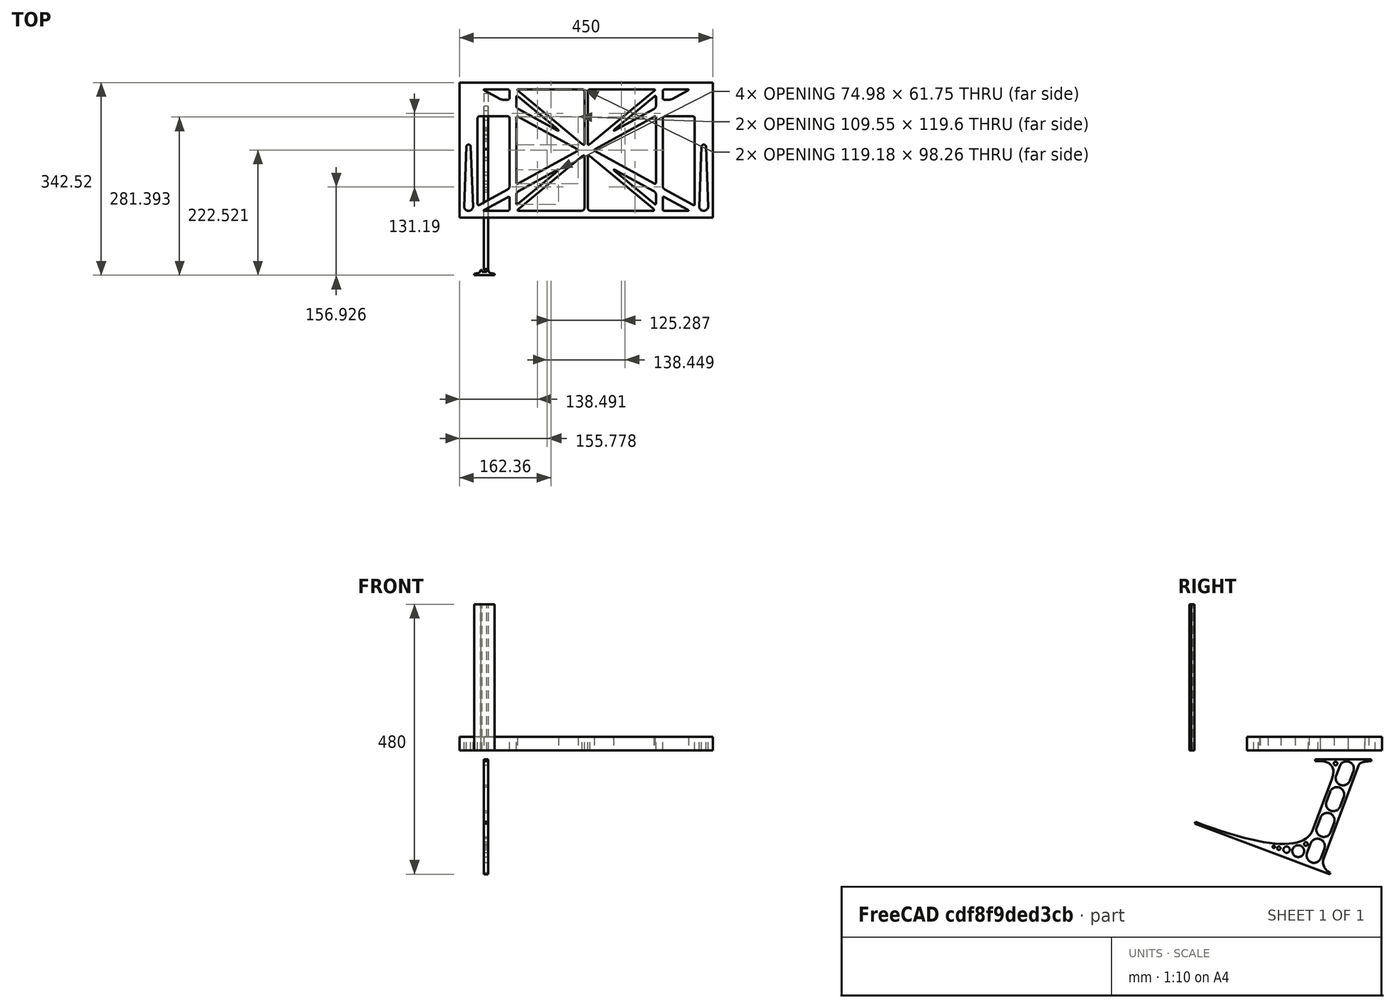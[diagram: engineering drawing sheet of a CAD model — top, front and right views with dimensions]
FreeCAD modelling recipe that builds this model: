
FCSTD DOCUMENT  (FreeCAD 0.19R0.19.2)
Label: laptopStand159FCStd
License: All rights reserved
LicenseURL: http://en.wikipedia.org/wiki/All_rights_reserved
objects: Sketcher::SketchObject×4, Part::Extrusion×3
note: 7 computed .brp shape members not serialized (recipe doc carries the construction recipe); baked Part::Feature solids carry a one-line shape summary decoded from their .brp

FEATURE [Sketcher::SketchObject] Sketch
  FullyConstrained = false
  sketch-geometry (349):
    g0: LineSegment StartX=-10.9272 StartY=-82.7794 StartZ=0 EndX=46.0728 EndY=-51.4823 EndZ=0
    g1: LineSegment StartX=-10.9272 StartY=76.4095 StartZ=0 EndX=-10.9272 EndY=-82.7794 EndZ=0
    g2: LineSegment StartX=46.0728 StartY=76.4095 StartZ=0 EndX=46.0728 EndY=-51.4823 EndZ=0
    g3: LineSegment StartX=-42.9272 StartY=136.221 StartZ=0 EndX=-42.9272 EndY=-103.779 EndZ=0
    g4: LineSegment StartX=407.073 StartY=136.221 StartZ=0 EndX=407.073 EndY=-103.779 EndZ=0
    g5: ArcOfCircle CenterX=-26.9272 CenterY=-83.7794 CenterZ=0 NormalX=0 NormalY=0 NormalZ=1 AngleXU=0 Radius=8 StartAngle=3.14159 EndAngle=6.28319
    g6: ArcOfCircle CenterX=391.073 CenterY=22.1087 CenterZ=0 NormalX=0 NormalY=0 NormalZ=1 AngleXU=0 Radius=8 StartAngle=-4.4e-15 EndAngle=3.14159
    g7: LineSegment StartX=399.073 StartY=22.1087 StartZ=0 EndX=399.073 EndY=-83.7794 EndZ=0
    g8: LineSegment StartX=383.073 StartY=22.1087 StartZ=0 EndX=383.073 EndY=-83.7794 EndZ=0
    g9: ArcOfCircle CenterX=391.073 CenterY=-83.7794 CenterZ=0 NormalX=0 NormalY=0 NormalZ=1 AngleXU=0 Radius=8 StartAngle=3.14159 EndAngle=6.28319
    g10: Circle CenterX=175.022 CenterY=27.0628 CenterZ=0 NormalX=0 NormalY=0 NormalZ=1 AngleXU=0 Radius=1
    g11: Circle CenterX=179.022 CenterY=24.8665 CenterZ=0 NormalX=0 NormalY=0 NormalZ=1 AngleXU=0 Radius=1
    g12: Circle CenterX=179.022 CenterY=27.0628 CenterZ=0 NormalX=0 NormalY=0 NormalZ=1 AngleXU=0 Radius=1
    g13: BSplineCurve PolesCount=3 KnotsCount=2 Degree=2 IsPeriodic=0
    g14: GeomPoint X=175.022 Y=27.0628 Z=0
    g15: GeomPoint X=179.022 Y=27.0628 Z=0
    g16: Circle CenterX=189.124 CenterY=27.0628 CenterZ=0 NormalX=0 NormalY=0 NormalZ=1 AngleXU=0 Radius=1
    g17: Circle CenterX=185.124 CenterY=24.8665 CenterZ=0 NormalX=0 NormalY=0 NormalZ=1 AngleXU=0 Radius=1
    g18: Circle CenterX=185.124 CenterY=27.0628 CenterZ=0 NormalX=0 NormalY=0 NormalZ=1 AngleXU=0 Radius=1
    g19: BSplineCurve PolesCount=3 KnotsCount=2 Degree=2 IsPeriodic=0
    g20: GeomPoint X=189.124 Y=27.0628 Z=0
    g21: GeomPoint X=185.124 Y=27.0628 Z=0
    g22: Circle CenterX=175.022 CenterY=5.37834 CenterZ=0 NormalX=0 NormalY=0 NormalZ=1 AngleXU=0 Radius=1
    g23: Circle CenterX=179.022 CenterY=7.57463 CenterZ=0 NormalX=0 NormalY=0 NormalZ=1 AngleXU=0 Radius=1
    g24: Circle CenterX=179.022 CenterY=5.34704 CenterZ=0 NormalX=0 NormalY=0 NormalZ=1 AngleXU=0 Radius=1
    g25: BSplineCurve PolesCount=3 KnotsCount=2 Degree=2 IsPeriodic=0
    g26: GeomPoint X=175.022 Y=5.37834 Z=0
    g27: GeomPoint X=179.022 Y=5.34704 Z=0
    g28: Circle CenterX=189.124 CenterY=5.37834 CenterZ=0 NormalX=0 NormalY=0 NormalZ=1 AngleXU=0 Radius=1
    g29: Circle CenterX=185.124 CenterY=7.57463 CenterZ=0 NormalX=0 NormalY=0 NormalZ=1 AngleXU=0 Radius=1
    g30: Circle CenterX=185.124 CenterY=5.34704 CenterZ=0 NormalX=0 NormalY=0 NormalZ=1 AngleXU=0 Radius=1
    g31: BSplineCurve PolesCount=3 KnotsCount=2 Degree=2 IsPeriodic=0
    g32: GeomPoint X=189.124 Y=5.37834 Z=0
    g33: GeomPoint X=185.124 Y=5.34704 Z=0
    g34: Circle CenterX=165.871 CenterY=18.1458 CenterZ=0 NormalX=0 NormalY=0 NormalZ=1 AngleXU=0 Radius=1
    g35: Circle CenterX=169.377 CenterY=16.2206 CenterZ=0 NormalX=0 NormalY=0 NormalZ=1 AngleXU=0 Radius=1
    g36: Circle CenterX=165.871 CenterY=14.2954 CenterZ=0 NormalX=0 NormalY=0 NormalZ=1 AngleXU=0 Radius=1
    g37: BSplineCurve PolesCount=3 KnotsCount=2 Degree=2 IsPeriodic=0
    g38: GeomPoint X=165.871 Y=18.1458 Z=0
    g39: GeomPoint X=165.871 Y=14.2954 Z=0
    g40: Circle CenterX=198.275 CenterY=18.1458 CenterZ=0 NormalX=0 NormalY=0 NormalZ=1 AngleXU=0 Radius=1
    g41: Circle CenterX=194.768 CenterY=16.2206 CenterZ=0 NormalX=0 NormalY=0 NormalZ=1 AngleXU=0 Radius=1
    g42: Circle CenterX=198.275 CenterY=14.2954 CenterZ=0 NormalX=0 NormalY=0 NormalZ=1 AngleXU=0 Radius=1
    g43: BSplineCurve PolesCount=3 KnotsCount=2 Degree=2 IsPeriodic=0
    g44: GeomPoint X=198.275 Y=18.1458 Z=0
    g45: GeomPoint X=198.275 Y=14.2954 Z=0
    g46: LineSegment StartX=407.073 StartY=-103.779 StartZ=0 EndX=-42.9272 EndY=-103.779 EndZ=0
    g47: LineSegment StartX=407.073 StartY=136.221 StartZ=0 EndX=-42.9272 EndY=136.221 EndZ=0
    g48: LineSegment StartX=46.0728 StartY=76.4095 StartZ=0 EndX=-10.9272 EndY=76.4095 EndZ=0
    g49: Circle CenterX=125.607 CenterY=54.1951 CenterZ=0 NormalX=0 NormalY=0 NormalZ=1 AngleXU=0 Radius=1
    g50: Circle CenterX=139.632 CenterY=46.4944 CenterZ=0 NormalX=0 NormalY=0 NormalZ=1 AngleXU=0 Radius=1
    g51: Circle CenterX=127.326 CenterY=56.7187 CenterZ=0 NormalX=0 NormalY=0 NormalZ=1 AngleXU=0 Radius=1
    g52: BSplineCurve PolesCount=3 KnotsCount=2 Degree=2 IsPeriodic=0
    g53: GeomPoint X=125.607 Y=54.1951 Z=0
    g54: GeomPoint X=127.326 Y=56.7187 Z=0
    g55: Circle CenterX=236.821 CenterY=56.7187 CenterZ=0 NormalX=0 NormalY=0 NormalZ=1 AngleXU=0 Radius=1
    g56: Circle CenterX=224.513 CenterY=46.4944 CenterZ=0 NormalX=0 NormalY=0 NormalZ=1 AngleXU=0 Radius=1
    g57: Circle CenterX=238.538 CenterY=54.1951 CenterZ=0 NormalX=0 NormalY=0 NormalZ=1 AngleXU=0 Radius=1
    g58: BSplineCurve PolesCount=3 KnotsCount=2 Degree=2 IsPeriodic=0
    g59: GeomPoint X=236.821 Y=56.7187 Z=0
    g60: GeomPoint X=238.538 Y=54.1951 Z=0
    g61: Circle CenterX=238.538 CenterY=-21.7539 CenterZ=0 NormalX=0 NormalY=0 NormalZ=1 AngleXU=0 Radius=1
    g62: Circle CenterX=224.513 CenterY=-14.0532 CenterZ=0 NormalX=0 NormalY=0 NormalZ=1 AngleXU=0 Radius=1
    g63: Circle CenterX=236.821 CenterY=-24.2775 CenterZ=0 NormalX=0 NormalY=0 NormalZ=1 AngleXU=0 Radius=1
    g64: BSplineCurve PolesCount=3 KnotsCount=2 Degree=2 IsPeriodic=0
    g65: GeomPoint X=238.538 Y=-21.7539 Z=0
    g66: GeomPoint X=236.821 Y=-24.2775 Z=0
    g67: Circle CenterX=125.607 CenterY=-21.7539 CenterZ=0 NormalX=0 NormalY=0 NormalZ=1 AngleXU=0 Radius=1
    g68: Circle CenterX=139.632 CenterY=-14.0532 CenterZ=0 NormalX=0 NormalY=0 NormalZ=1 AngleXU=0 Radius=1
    g69: Circle CenterX=127.325 CenterY=-24.2775 CenterZ=0 NormalX=0 NormalY=0 NormalZ=1 AngleXU=0 Radius=1
    g70: BSplineCurve PolesCount=3 KnotsCount=2 Degree=2 IsPeriodic=0
    g71: GeomPoint X=125.607 Y=-21.7539 Z=0
    g72: GeomPoint X=127.325 Y=-24.2775 Z=0
    g73: Circle CenterX=302.996 CenterY=111.695 CenterZ=0 NormalX=0 NormalY=0 NormalZ=1 AngleXU=0 Radius=1
    g74: Circle CenterX=306.073 CenterY=114.251 CenterZ=0 NormalX=0 NormalY=0 NormalZ=1 AngleXU=0 Radius=1
    g75: Circle CenterX=306.073 CenterY=110.251 CenterZ=0 NormalX=0 NormalY=0 NormalZ=1 AngleXU=0 Radius=1
    g76: BSplineCurve PolesCount=3 KnotsCount=2 Degree=2 IsPeriodic=0
    g77: GeomPoint X=302.996 Y=111.695 Z=0
    g78: GeomPoint X=306.073 Y=110.251 Z=0
    g79: Circle CenterX=306.073 CenterY=95.2763 CenterZ=0 NormalX=0 NormalY=0 NormalZ=1 AngleXU=0 Radius=1
    g80: Circle CenterX=306.073 CenterY=91.2763 CenterZ=0 NormalX=0 NormalY=0 NormalZ=1 AngleXU=0 Radius=1
    g81: Circle CenterX=302.567 CenterY=89.3511 CenterZ=0 NormalX=0 NormalY=0 NormalZ=1 AngleXU=0 Radius=1
    g82: BSplineCurve PolesCount=3 KnotsCount=2 Degree=2 IsPeriodic=0
    g83: GeomPoint X=306.073 Y=95.2763 Z=0
    g84: GeomPoint X=302.567 Y=89.3511 Z=0
    g85: LineSegment StartX=306.073 StartY=110.251 StartZ=0 EndX=306.073 EndY=95.2763 EndZ=0
    g86: LineSegment StartX=302.996 StartY=111.695 StartZ=0 EndX=236.821 EndY=56.7187 EndZ=0
    g87: LineSegment StartX=238.538 StartY=54.1951 StartZ=0 EndX=302.567 EndY=89.3511 EndZ=0
    g88: Circle CenterX=61.1496 CenterY=111.695 CenterZ=0 NormalX=0 NormalY=0 NormalZ=1 AngleXU=0 Radius=1
    g89: Circle CenterX=58.0728 CenterY=114.251 CenterZ=0 NormalX=0 NormalY=0 NormalZ=1 AngleXU=0 Radius=1
    g90: Circle CenterX=58.0728 CenterY=110.251 CenterZ=0 NormalX=0 NormalY=0 NormalZ=1 AngleXU=0 Radius=1
    g91: BSplineCurve PolesCount=3 KnotsCount=2 Degree=2 IsPeriodic=0
    g92: GeomPoint X=61.1496 Y=111.695 Z=0
    g93: GeomPoint X=58.0728 Y=110.251 Z=0
    g94: Circle CenterX=61.5791 CenterY=89.3511 CenterZ=0 NormalX=0 NormalY=0 NormalZ=1 AngleXU=0 Radius=1
    g95: Circle CenterX=58.0728 CenterY=91.2763 CenterZ=0 NormalX=0 NormalY=0 NormalZ=1 AngleXU=0 Radius=1
    g96: Circle CenterX=58.0728 CenterY=95.2763 CenterZ=0 NormalX=0 NormalY=0 NormalZ=1 AngleXU=0 Radius=1
    g97: BSplineCurve PolesCount=3 KnotsCount=2 Degree=2 IsPeriodic=0
    g98: GeomPoint X=61.5791 Y=89.3511 Z=0
    g99: GeomPoint X=58.0728 Y=95.2763 Z=0
    g100: LineSegment StartX=58.0728 StartY=110.251 StartZ=0 EndX=58.0728 EndY=95.2763 EndZ=0
    g101: LineSegment StartX=61.1496 StartY=111.695 StartZ=0 EndX=127.326 EndY=56.7187 EndZ=0
    g102: LineSegment StartX=125.607 StartY=54.1951 StartZ=0 EndX=61.5791 EndY=89.3511 EndZ=0
    g103: Circle CenterX=61.5791 CenterY=-56.9099 CenterZ=0 NormalX=0 NormalY=0 NormalZ=1 AngleXU=0 Radius=1
    g104: Circle CenterX=58.0728 CenterY=-58.8351 CenterZ=0 NormalX=0 NormalY=0 NormalZ=1 AngleXU=0 Radius=1
    g105: Circle CenterX=58.0728 CenterY=-62.8351 CenterZ=0 NormalX=0 NormalY=0 NormalZ=1 AngleXU=0 Radius=1
    g106: BSplineCurve PolesCount=3 KnotsCount=2 Degree=2 IsPeriodic=0
    g107: GeomPoint X=61.5791 Y=-56.9099 Z=0
    g108: GeomPoint X=58.0728 Y=-62.8351 Z=0
    g109: Circle CenterX=58.0728 CenterY=-77.8102 CenterZ=0 NormalX=0 NormalY=0 NormalZ=1 AngleXU=0 Radius=1
    g110: Circle CenterX=58.0728 CenterY=-81.8102 CenterZ=0 NormalX=0 NormalY=0 NormalZ=1 AngleXU=0 Radius=1
    g111: Circle CenterX=61.1496 CenterY=-79.2541 CenterZ=0 NormalX=0 NormalY=0 NormalZ=1 AngleXU=0 Radius=1
    g112: BSplineCurve PolesCount=3 KnotsCount=2 Degree=2 IsPeriodic=0
    g113: GeomPoint X=58.0728 Y=-77.8102 Z=0
    g114: GeomPoint X=61.1496 Y=-79.2541 Z=0
    g115: LineSegment StartX=58.0728 StartY=-62.8351 StartZ=0 EndX=58.0728 EndY=-77.8102 EndZ=0
    g116: LineSegment StartX=61.1496 StartY=-79.2541 StartZ=0 EndX=127.325 EndY=-24.2775 EndZ=0
    g117: LineSegment StartX=125.607 StartY=-21.7539 StartZ=0 EndX=61.5791 EndY=-56.9099 EndZ=0
    g118: Circle CenterX=302.567 CenterY=-56.9099 CenterZ=0 NormalX=0 NormalY=0 NormalZ=1 AngleXU=0 Radius=1
    g119: Circle CenterX=306.073 CenterY=-58.8351 CenterZ=0 NormalX=0 NormalY=0 NormalZ=1 AngleXU=0 Radius=1
    g120: Circle CenterX=306.073 CenterY=-62.8351 CenterZ=0 NormalX=0 NormalY=0 NormalZ=1 AngleXU=0 Radius=1
    g121: BSplineCurve PolesCount=3 KnotsCount=2 Degree=2 IsPeriodic=0
    g122: GeomPoint X=302.567 Y=-56.9099 Z=0
    g123: GeomPoint X=306.073 Y=-62.8351 Z=0
    g124: Circle CenterX=302.996 CenterY=-79.2541 CenterZ=0 NormalX=0 NormalY=0 NormalZ=1 AngleXU=0 Radius=1
    g125: Circle CenterX=306.073 CenterY=-81.8102 CenterZ=0 NormalX=0 NormalY=0 NormalZ=1 AngleXU=0 Radius=1
    g126: Circle CenterX=306.073 CenterY=-77.8102 CenterZ=0 NormalX=0 NormalY=0 NormalZ=1 AngleXU=0 Radius=1
    g127: BSplineCurve PolesCount=3 KnotsCount=2 Degree=2 IsPeriodic=0
    g128: GeomPoint X=302.996 Y=-79.2541 Z=0
    g129: GeomPoint X=306.073 Y=-77.8102 Z=0
    g130: LineSegment StartX=306.073 StartY=-62.8351 StartZ=0 EndX=306.073 EndY=-77.8102 EndZ=0
    g131: LineSegment StartX=302.996 StartY=-79.2541 StartZ=0 EndX=236.821 EndY=-24.2775 EndZ=0
    g132: LineSegment StartX=238.538 StartY=-21.7539 StartZ=0 EndX=302.567 EndY=-56.9099 EndZ=0
    g133: Circle CenterX=61.6457 CenterY=-88.8112 CenterZ=0 NormalX=0 NormalY=0 NormalZ=1 AngleXU=0 Radius=1
    g134: Circle CenterX=58.0728 CenterY=-91.7794 CenterZ=0 NormalX=0 NormalY=0 NormalZ=1 AngleXU=0 Radius=1
    g135: Circle CenterX=63.9135 CenterY=-91.7794 CenterZ=0 NormalX=0 NormalY=0 NormalZ=1 AngleXU=0 Radius=1
    g136: BSplineCurve PolesCount=3 KnotsCount=2 Degree=2 IsPeriodic=0
    g137: GeomPoint X=61.6457 Y=-88.8112 Z=0
    g138: GeomPoint X=63.9135 Y=-91.7794 Z=0
    g139: Circle CenterX=179.022 CenterY=-85.8163 CenterZ=0 NormalX=0 NormalY=0 NormalZ=1 AngleXU=0 Radius=1
    g140: Circle CenterX=179.022 CenterY=-91.7794 CenterZ=0 NormalX=0 NormalY=0 NormalZ=1 AngleXU=0 Radius=1
    g141: Circle CenterX=171.895 CenterY=-91.7794 CenterZ=0 NormalX=0 NormalY=0 NormalZ=1 AngleXU=0 Radius=1
    g142: BSplineCurve PolesCount=3 KnotsCount=2 Degree=2 IsPeriodic=0
    g143: GeomPoint X=179.022 Y=-85.8163 Z=0
    g144: GeomPoint X=171.895 Y=-91.7794 Z=0
    g145: Circle CenterX=185.124 CenterY=-86.2028 CenterZ=0 NormalX=0 NormalY=0 NormalZ=1 AngleXU=0 Radius=1
    g146: Circle CenterX=185.124 CenterY=-91.7794 CenterZ=0 NormalX=0 NormalY=0 NormalZ=1 AngleXU=0 Radius=1
    g147: Circle CenterX=191.747 CenterY=-91.7794 CenterZ=0 NormalX=0 NormalY=0 NormalZ=1 AngleXU=0 Radius=1
    g148: BSplineCurve PolesCount=3 KnotsCount=2 Degree=2 IsPeriodic=0
    g149: GeomPoint X=185.124 Y=-86.2028 Z=0
    g150: GeomPoint X=191.747 Y=-91.7794 Z=0
    g151: Circle CenterX=299.888 CenterY=-86.6413 CenterZ=0 NormalX=0 NormalY=0 NormalZ=1 AngleXU=0 Radius=1
    g152: Circle CenterX=306.073 CenterY=-91.7794 CenterZ=0 NormalX=0 NormalY=0 NormalZ=1 AngleXU=0 Radius=1
    g153: Circle CenterX=298.776 CenterY=-91.7794 CenterZ=0 NormalX=0 NormalY=0 NormalZ=1 AngleXU=0 Radius=1
    g154: BSplineCurve PolesCount=3 KnotsCount=2 Degree=2 IsPeriodic=0
    g155: GeomPoint X=299.888 Y=-86.6413 Z=0
    g156: GeomPoint X=298.776 Y=-91.7794 Z=0
    g157: LineSegment StartX=189.124 StartY=5.37834 StartZ=0 EndX=299.888 EndY=-86.6413 EndZ=0
    g158: LineSegment StartX=298.776 StartY=-91.7794 StartZ=0 EndX=191.747 EndY=-91.7794 EndZ=0
    g159: LineSegment StartX=185.124 StartY=-86.2028 StartZ=0 EndX=185.124 EndY=5.34704 EndZ=0
    g160: LineSegment StartX=179.022 StartY=5.34704 StartZ=0 EndX=179.022 EndY=-85.8163 EndZ=0
    g161: LineSegment StartX=171.895 StartY=-91.7794 StartZ=0 EndX=63.9135 EndY=-91.7794 EndZ=0
    g162: LineSegment StartX=61.6457 StartY=-88.8112 StartZ=0 EndX=175.022 EndY=5.37834 EndZ=0
    g163: Circle CenterX=302.073 CenterY=124.221 CenterZ=0 NormalX=0 NormalY=0 NormalZ=1 AngleXU=0 Radius=1
    g164: Circle CenterX=306.073 CenterY=124.221 CenterZ=0 NormalX=0 NormalY=0 NormalZ=1 AngleXU=0 Radius=1
    g165: Circle CenterX=302.996 CenterY=121.665 CenterZ=0 NormalX=0 NormalY=0 NormalZ=1 AngleXU=0 Radius=1
    g166: BSplineCurve PolesCount=3 KnotsCount=2 Degree=2 IsPeriodic=0
    g167: GeomPoint X=302.073 Y=124.221 Z=0
    g168: GeomPoint X=302.996 Y=121.665 Z=0
    g169: Circle CenterX=189.124 CenterY=124.221 CenterZ=0 NormalX=0 NormalY=0 NormalZ=1 AngleXU=0 Radius=1
    g170: Circle CenterX=185.124 CenterY=124.221 CenterZ=0 NormalX=0 NormalY=0 NormalZ=1 AngleXU=0 Radius=1
    g171: Circle CenterX=185.124 CenterY=120.221 CenterZ=0 NormalX=0 NormalY=0 NormalZ=1 AngleXU=0 Radius=1
    g172: BSplineCurve PolesCount=3 KnotsCount=2 Degree=2 IsPeriodic=0
    g173: GeomPoint X=189.124 Y=124.221 Z=0
    g174: GeomPoint X=185.124 Y=120.221 Z=0
    g175: Circle CenterX=175.022 CenterY=124.221 CenterZ=0 NormalX=0 NormalY=0 NormalZ=1 AngleXU=0 Radius=1
    g176: Circle CenterX=179.022 CenterY=124.221 CenterZ=0 NormalX=0 NormalY=0 NormalZ=1 AngleXU=0 Radius=1
    g177: Circle CenterX=179.022 CenterY=120.221 CenterZ=0 NormalX=0 NormalY=0 NormalZ=1 AngleXU=0 Radius=1
    g178: BSplineCurve PolesCount=3 KnotsCount=2 Degree=2 IsPeriodic=0
    g179: GeomPoint X=175.022 Y=124.221 Z=0
    g180: GeomPoint X=179.022 Y=120.221 Z=0
    g181: Circle CenterX=62.0728 CenterY=124.221 CenterZ=0 NormalX=0 NormalY=0 NormalZ=1 AngleXU=0 Radius=1
    g182: Circle CenterX=58.0728 CenterY=124.221 CenterZ=0 NormalX=0 NormalY=0 NormalZ=1 AngleXU=0 Radius=1
    g183: Circle CenterX=61.1496 CenterY=121.665 CenterZ=0 NormalX=0 NormalY=0 NormalZ=1 AngleXU=0 Radius=1
    g184: BSplineCurve PolesCount=3 KnotsCount=2 Degree=2 IsPeriodic=0
    g185: GeomPoint X=62.0728 Y=124.221 Z=0
    g186: GeomPoint X=61.1496 Y=121.665 Z=0
    g187: LineSegment StartX=62.0728 StartY=124.221 StartZ=0 EndX=175.022 EndY=124.221 EndZ=0
    g188: LineSegment StartX=179.022 StartY=120.221 StartZ=0 EndX=179.022 EndY=27.0628 EndZ=0
    g189: LineSegment StartX=185.124 StartY=27.0628 StartZ=0 EndX=185.124 EndY=120.221 EndZ=0
    g190: LineSegment StartX=189.124 StartY=124.221 StartZ=0 EndX=302.073 EndY=124.221 EndZ=0
    g191: LineSegment StartX=302.996 StartY=121.665 StartZ=0 EndX=189.124 EndY=27.0628 EndZ=0
    g192: LineSegment StartX=175.022 StartY=27.0628 StartZ=0 EndX=61.1496 EndY=121.665 EndZ=0
    g193: Circle CenterX=61.5791 CenterY=75.4095 CenterZ=0 NormalX=0 NormalY=0 NormalZ=1 AngleXU=0 Radius=1
    g194: Circle CenterX=58.0728 CenterY=77.3346 CenterZ=0 NormalX=0 NormalY=0 NormalZ=1 AngleXU=0 Radius=1
    g195: Circle CenterX=58.0728 CenterY=73.3346 CenterZ=0 NormalX=0 NormalY=0 NormalZ=1 AngleXU=0 Radius=1
    g196: BSplineCurve PolesCount=3 KnotsCount=2 Degree=2 IsPeriodic=0
    g197: GeomPoint X=61.5791 Y=75.4095 Z=0
    g198: GeomPoint X=58.0728 Y=73.3346 Z=0
    g199: Circle CenterX=58.0728 CenterY=-40.8935 CenterZ=0 NormalX=0 NormalY=0 NormalZ=1 AngleXU=0 Radius=1
    g200: Circle CenterX=58.0728 CenterY=-44.8935 CenterZ=0 NormalX=0 NormalY=0 NormalZ=1 AngleXU=0 Radius=1
    g201: Circle CenterX=61.5791 CenterY=-42.9683 CenterZ=0 NormalX=0 NormalY=0 NormalZ=1 AngleXU=0 Radius=1
    g202: BSplineCurve PolesCount=3 KnotsCount=2 Degree=2 IsPeriodic=0
    g203: GeomPoint X=58.0728 Y=-40.8935 Z=0
    g204: GeomPoint X=61.5791 Y=-42.9683 Z=0
    g205: LineSegment StartX=61.5791 StartY=-42.9683 StartZ=0 EndX=165.871 EndY=14.2954 EndZ=0
    g206: LineSegment StartX=165.871 StartY=18.1458 StartZ=0 EndX=61.5791 EndY=75.4095 EndZ=0
    g207: LineSegment StartX=58.0728 StartY=73.3346 StartZ=0 EndX=58.0728 EndY=-40.8935 EndZ=0
    g208: Circle CenterX=302.567 CenterY=-42.9683 CenterZ=0 NormalX=0 NormalY=0 NormalZ=1 AngleXU=0 Radius=1
    g209: Circle CenterX=306.073 CenterY=-44.8935 CenterZ=0 NormalX=0 NormalY=0 NormalZ=1 AngleXU=0 Radius=1
    g210: Circle CenterX=306.073 CenterY=-40.8935 CenterZ=0 NormalX=0 NormalY=0 NormalZ=1 AngleXU=0 Radius=1
    g211: BSplineCurve PolesCount=3 KnotsCount=2 Degree=2 IsPeriodic=0
    g212: GeomPoint X=302.567 Y=-42.9683 Z=0
    g213: GeomPoint X=306.073 Y=-40.8935 Z=0
    g214: Circle CenterX=306.073 CenterY=73.3346 CenterZ=0 NormalX=0 NormalY=0 NormalZ=1 AngleXU=0 Radius=1
    g215: Circle CenterX=306.073 CenterY=77.3346 CenterZ=0 NormalX=0 NormalY=0 NormalZ=1 AngleXU=0 Radius=1
    g216: Circle CenterX=302.567 CenterY=75.4095 CenterZ=0 NormalX=0 NormalY=0 NormalZ=1 AngleXU=0 Radius=1
    g217: BSplineCurve PolesCount=3 KnotsCount=2 Degree=2 IsPeriodic=0
    g218: GeomPoint X=306.073 Y=73.3346 Z=0
    g219: GeomPoint X=302.567 Y=75.4095 Z=0
    g220: LineSegment StartX=302.567 StartY=-42.9683 StartZ=0 EndX=198.275 EndY=14.2954 EndZ=0
    g221: LineSegment StartX=198.275 StartY=18.1458 StartZ=0 EndX=302.567 EndY=75.4095 EndZ=0
    g222: LineSegment StartX=306.073 StartY=73.3346 StartZ=0 EndX=306.073 EndY=-40.8935 EndZ=0
    g223: LineSegment StartX=322.073 StartY=105.865 StartZ=0 EndX=328.643 EndY=105.865 EndZ=0
    g224: LineSegment StartX=318.073 StartY=120.221 StartZ=0 EndX=318.073 EndY=109.865 EndZ=0
    g225: LineSegment StartX=336.157 StartY=107.779 StartZ=0 EndX=362.567 EndY=122.294 EndZ=0
    g226: Circle CenterX=362.073 CenterY=124.221 CenterZ=0 NormalX=0 NormalY=0 NormalZ=1 AngleXU=0 Radius=1
    g227: Circle CenterX=366.073 CenterY=124.221 CenterZ=0 NormalX=0 NormalY=0 NormalZ=1 AngleXU=0 Radius=1
    g228: Circle CenterX=362.567 CenterY=122.294 CenterZ=0 NormalX=0 NormalY=0 NormalZ=1 AngleXU=0 Radius=1
    g229: BSplineCurve PolesCount=3 KnotsCount=2 Degree=2 IsPeriodic=0
    g230: GeomPoint X=362.073 Y=124.221 Z=0
    g231: GeomPoint X=362.567 Y=122.294 Z=0
    g232: Circle CenterX=322.073 CenterY=124.221 CenterZ=0 NormalX=0 NormalY=0 NormalZ=1 AngleXU=0 Radius=1
    g233: Circle CenterX=318.073 CenterY=124.221 CenterZ=0 NormalX=0 NormalY=0 NormalZ=1 AngleXU=0 Radius=1
    g234: Circle CenterX=318.073 CenterY=120.221 CenterZ=0 NormalX=0 NormalY=0 NormalZ=1 AngleXU=0 Radius=1
    g235: BSplineCurve PolesCount=3 KnotsCount=2 Degree=2 IsPeriodic=0
    g236: GeomPoint X=322.073 Y=124.221 Z=0
    g237: GeomPoint X=318.073 Y=120.221 Z=0
    g238: Circle CenterX=322.073 CenterY=105.865 CenterZ=0 NormalX=0 NormalY=0 NormalZ=1 AngleXU=0 Radius=1
    g239: Circle CenterX=318.073 CenterY=105.865 CenterZ=0 NormalX=0 NormalY=0 NormalZ=1 AngleXU=0 Radius=1
    g240: Circle CenterX=318.073 CenterY=109.865 CenterZ=0 NormalX=0 NormalY=0 NormalZ=1 AngleXU=0 Radius=1
    g241: BSplineCurve PolesCount=3 KnotsCount=2 Degree=2 IsPeriodic=0
    g242: GeomPoint X=322.073 Y=105.865 Z=0
    g243: GeomPoint X=318.073 Y=109.865 Z=0
    g244: Circle CenterX=336.157 CenterY=107.779 CenterZ=0 NormalX=0 NormalY=0 NormalZ=1 AngleXU=0 Radius=1
    g245: Circle CenterX=332.651 CenterY=105.853 CenterZ=0 NormalX=0 NormalY=0 NormalZ=1 AngleXU=0 Radius=1
    g246: Circle CenterX=328.643 CenterY=105.865 CenterZ=0 NormalX=0 NormalY=0 NormalZ=1 AngleXU=0 Radius=1
    g247: BSplineCurve PolesCount=3 KnotsCount=2 Degree=2 IsPeriodic=0
    g248: GeomPoint X=336.157 Y=107.779 Z=0
    g249: GeomPoint X=328.643 Y=105.865 Z=0
    g250: LineSegment StartX=322.073 StartY=124.221 StartZ=0 EndX=362.073 EndY=124.221 EndZ=0
    g251: Circle CenterX=371.567 CenterY=-80.8644 CenterZ=0 NormalX=0 NormalY=0 NormalZ=1 AngleXU=0 Radius=1
    g252: Circle CenterX=375.073 CenterY=-82.7896 CenterZ=0 NormalX=0 NormalY=0 NormalZ=1 AngleXU=0 Radius=1
    g253: Circle CenterX=375.073 CenterY=-78.7896 CenterZ=0 NormalX=0 NormalY=0 NormalZ=1 AngleXU=0 Radius=1
    g254: BSplineCurve PolesCount=3 KnotsCount=2 Degree=2 IsPeriodic=0
    g255: GeomPoint X=371.567 Y=-80.8644 Z=0
    g256: GeomPoint X=375.073 Y=-78.7896 Z=0
    g257: Circle CenterX=321.579 CenterY=-53.4075 CenterZ=0 NormalX=0 NormalY=0 NormalZ=1 AngleXU=0 Radius=1
    g258: Circle CenterX=318.073 CenterY=-51.4823 CenterZ=0 NormalX=0 NormalY=0 NormalZ=1 AngleXU=0 Radius=1
    g259: Circle CenterX=318.073 CenterY=-47.4805 CenterZ=0 NormalX=0 NormalY=0 NormalZ=1 AngleXU=0 Radius=1
    g260: BSplineCurve PolesCount=3 KnotsCount=2 Degree=2 IsPeriodic=0
    g261: GeomPoint X=321.579 Y=-53.4075 Z=0
    g262: GeomPoint X=318.073 Y=-47.4805 Z=0
    g263: LineSegment StartX=371.567 StartY=-80.8644 StartZ=0 EndX=321.579 EndY=-53.4075 EndZ=0
    g264: Circle CenterX=321.579 CenterY=-67.3492 CenterZ=0 NormalX=0 NormalY=0 NormalZ=1 AngleXU=0 Radius=1
    g265: Circle CenterX=318.073 CenterY=-65.424 CenterZ=0 NormalX=0 NormalY=0 NormalZ=1 AngleXU=0 Radius=1
    g266: Circle CenterX=318.073 CenterY=-69.424 CenterZ=0 NormalX=0 NormalY=0 NormalZ=1 AngleXU=0 Radius=1
    g267: BSplineCurve PolesCount=3 KnotsCount=2 Degree=2 IsPeriodic=0
    g268: GeomPoint X=321.579 Y=-67.3492 Z=0
    g269: GeomPoint X=318.073 Y=-69.424 Z=0
    g270: Circle CenterX=362.567 CenterY=-89.8542 CenterZ=0 NormalX=0 NormalY=0 NormalZ=1 AngleXU=0 Radius=1
    g271: Circle CenterX=366.073 CenterY=-91.7794 CenterZ=0 NormalX=0 NormalY=0 NormalZ=1 AngleXU=0 Radius=1
    g272: Circle CenterX=362.073 CenterY=-91.7794 CenterZ=0 NormalX=0 NormalY=0 NormalZ=1 AngleXU=0 Radius=1
    g273: BSplineCurve PolesCount=3 KnotsCount=2 Degree=2 IsPeriodic=0
    g274: GeomPoint X=362.567 Y=-89.8542 Z=0
    g275: GeomPoint X=362.073 Y=-91.7794 Z=0
    g276: Circle CenterX=322.073 CenterY=-91.7794 CenterZ=0 NormalX=0 NormalY=0 NormalZ=1 AngleXU=0 Radius=1
    g277: Circle CenterX=318.073 CenterY=-91.7794 CenterZ=0 NormalX=0 NormalY=0 NormalZ=1 AngleXU=0 Radius=1
    g278: Circle CenterX=318.073 CenterY=-87.7794 CenterZ=0 NormalX=0 NormalY=0 NormalZ=1 AngleXU=0 Radius=1
    g279: BSplineCurve PolesCount=3 KnotsCount=2 Degree=2 IsPeriodic=0
    g280: GeomPoint X=322.073 Y=-91.7794 Z=0
    g281: GeomPoint X=318.073 Y=-87.7794 Z=0
    g282: LineSegment StartX=362.567 StartY=-89.8542 StartZ=0 EndX=321.579 EndY=-67.3492 EndZ=0
    g283: LineSegment StartX=318.073 StartY=-69.424 StartZ=0 EndX=318.073 EndY=-87.7794 EndZ=0
    g284: LineSegment StartX=322.073 StartY=-91.7794 StartZ=0 EndX=362.073 EndY=-91.7794 EndZ=0
    g285: Circle CenterX=2.07281 CenterY=124.221 CenterZ=0 NormalX=0 NormalY=0 NormalZ=1 AngleXU=0 Radius=1
    g286: Circle CenterX=1.57905 CenterY=122.295 CenterZ=0 NormalX=0 NormalY=0 NormalZ=1 AngleXU=0 Radius=1
    g287: BSplineCurve PolesCount=3 KnotsCount=2 Degree=2 IsPeriodic=0
    g288: GeomPoint X=2.07281 Y=124.221 Z=0
    g289: GeomPoint X=1.57905 Y=122.295 Z=0
    g290: Circle CenterX=42.0728 CenterY=124.221 CenterZ=0 NormalX=0 NormalY=0 NormalZ=1 AngleXU=0 Radius=1
    g291: Circle CenterX=46.0728 CenterY=124.221 CenterZ=0 NormalX=0 NormalY=0 NormalZ=1 AngleXU=0 Radius=1
    g292: Circle CenterX=46.0728 CenterY=120.221 CenterZ=0 NormalX=0 NormalY=0 NormalZ=1 AngleXU=0 Radius=1
    g293: BSplineCurve PolesCount=3 KnotsCount=2 Degree=2 IsPeriodic=0
    g294: GeomPoint X=42.0728 Y=124.221 Z=0
    g295: GeomPoint X=46.0728 Y=120.221 Z=0
    g296: Circle CenterX=46.0728 CenterY=109.865 CenterZ=0 NormalX=0 NormalY=0 NormalZ=1 AngleXU=0 Radius=1
    g297: Circle CenterX=46.0728 CenterY=105.865 CenterZ=0 NormalX=0 NormalY=0 NormalZ=1 AngleXU=0 Radius=1
    g298: Circle CenterX=42.0728 CenterY=105.865 CenterZ=0 NormalX=0 NormalY=0 NormalZ=1 AngleXU=0 Radius=1
    g299: BSplineCurve PolesCount=3 KnotsCount=2 Degree=2 IsPeriodic=0
    g300: GeomPoint X=46.0728 Y=109.865 Z=0
    g301: GeomPoint X=42.0728 Y=105.865 Z=0
    g302: Circle CenterX=35.5028 CenterY=105.865 CenterZ=0 NormalX=0 NormalY=0 NormalZ=1 AngleXU=0 Radius=1
    g303: Circle CenterX=31.5028 CenterY=105.865 CenterZ=0 NormalX=0 NormalY=0 NormalZ=1 AngleXU=0 Radius=1
    g304: Circle CenterX=27.9965 CenterY=107.79 CenterZ=0 NormalX=0 NormalY=0 NormalZ=1 AngleXU=0 Radius=1
    g305: BSplineCurve PolesCount=3 KnotsCount=2 Degree=2 IsPeriodic=0
    g306: GeomPoint X=35.5028 Y=105.865 Z=0
    g307: GeomPoint X=27.9965 Y=107.79 Z=0
    g308: LineSegment StartX=2.07281 StartY=124.221 StartZ=0 EndX=42.0728 EndY=124.221 EndZ=0
    g309: LineSegment StartX=46.0728 StartY=120.221 StartZ=0 EndX=46.0728 EndY=109.865 EndZ=0
    g310: LineSegment StartX=42.0728 StartY=105.865 StartZ=0 EndX=35.5028 EndY=105.865 EndZ=0
    g311: LineSegment StartX=27.9965 StartY=107.79 StartZ=0 EndX=1.57905 EndY=122.295 EndZ=0
    g312: Circle CenterX=42.5666 CenterY=-67.3492 CenterZ=0 NormalX=0 NormalY=0 NormalZ=1 AngleXU=0 Radius=1
    g313: Circle CenterX=46.0728 CenterY=-65.424 CenterZ=0 NormalX=0 NormalY=0 NormalZ=1 AngleXU=0 Radius=1
    g314: Circle CenterX=46.0728 CenterY=-69.424 CenterZ=0 NormalX=0 NormalY=0 NormalZ=1 AngleXU=0 Radius=1
    g315: BSplineCurve PolesCount=3 KnotsCount=2 Degree=2 IsPeriodic=0
    g316: GeomPoint X=42.5666 Y=-67.3492 Z=0
    g317: GeomPoint X=46.0728 Y=-69.424 Z=0
    g318: Circle CenterX=46.0728 CenterY=-87.7794 CenterZ=0 NormalX=0 NormalY=0 NormalZ=1 AngleXU=0 Radius=1
    g319: Circle CenterX=46.0728 CenterY=-91.7794 CenterZ=0 NormalX=0 NormalY=0 NormalZ=1 AngleXU=0 Radius=1
    g320: Circle CenterX=42.0728 CenterY=-91.7794 CenterZ=0 NormalX=0 NormalY=0 NormalZ=1 AngleXU=0 Radius=1
    g321: BSplineCurve PolesCount=3 KnotsCount=2 Degree=2 IsPeriodic=0
    g322: GeomPoint X=46.0728 Y=-87.7794 Z=0
    g323: GeomPoint X=42.0728 Y=-91.7794 Z=0
    g324: Circle CenterX=2.07281 CenterY=-91.7794 CenterZ=0 NormalX=0 NormalY=0 NormalZ=1 AngleXU=0 Radius=1
    g325: Circle CenterX=-1.92719 CenterY=-91.7794 CenterZ=0 NormalX=0 NormalY=0 NormalZ=1 AngleXU=0 Radius=1
    g326: Circle CenterX=1.57905 CenterY=-89.8542 CenterZ=0 NormalX=0 NormalY=0 NormalZ=1 AngleXU=0 Radius=1
    g327: BSplineCurve PolesCount=3 KnotsCount=2 Degree=2 IsPeriodic=0
    g328: GeomPoint X=2.07281 Y=-91.7794 Z=0
    g329: GeomPoint X=1.57905 Y=-89.8542 Z=0
    g330: LineSegment StartX=2.07281 StartY=-91.7794 StartZ=0 EndX=42.0728 EndY=-91.7794 EndZ=0
    g331: LineSegment StartX=46.0728 StartY=-87.7794 StartZ=0 EndX=46.0728 EndY=-69.424 EndZ=0
    g332: LineSegment StartX=42.5666 StartY=-67.3492 StartZ=0 EndX=1.57905 EndY=-89.8542 EndZ=0
    g333: Circle CenterX=322.073 CenterY=76.4095 CenterZ=0 NormalX=0 NormalY=0 NormalZ=1 AngleXU=0 Radius=4
    g334: BSplineCurve PolesCount=3 KnotsCount=2 Degree=2 IsPeriodic=0
    g335: GeomPoint X=318.073 Y=72.4095 Z=0
    g336: GeomPoint X=322.073 Y=76.4095 Z=0
    g337: Circle CenterX=375.073 CenterY=72.4095 CenterZ=0 NormalX=0 NormalY=0 NormalZ=1 AngleXU=0 Radius=1
    g338: Circle CenterX=375.073 CenterY=76.4095 CenterZ=0 NormalX=0 NormalY=0 NormalZ=1 AngleXU=0 Radius=1
    g339: Circle CenterX=371.073 CenterY=76.4095 CenterZ=0 NormalX=0 NormalY=0 NormalZ=1 AngleXU=0 Radius=1
    g340: BSplineCurve PolesCount=3 KnotsCount=2 Degree=2 IsPeriodic=0
    g341: GeomPoint X=375.073 Y=72.4095 Z=0
    g342: GeomPoint X=371.073 Y=76.4095 Z=0
    g343: LineSegment StartX=322.073 StartY=76.4095 StartZ=0 EndX=371.073 EndY=76.4095 EndZ=0
    g344: LineSegment StartX=318.073 StartY=72.4095 StartZ=0 EndX=318.073 EndY=-47.4805 EndZ=0
    g345: LineSegment StartX=375.073 StartY=72.4095 StartZ=0 EndX=375.073 EndY=-78.7896 EndZ=0
    g346: ArcOfCircle CenterX=-26.9272 CenterY=22.1087 CenterZ=0 NormalX=0 NormalY=0 NormalZ=1 AngleXU=0 Radius=4 StartAngle=5e-16 EndAngle=3.14159
    g347: LineSegment StartX=-30.9272 StartY=22.1087 StartZ=0 EndX=-34.9272 EndY=-83.7794 EndZ=0
    g348: LineSegment StartX=-18.9272 StartY=-83.7794 StartZ=0 EndX=-22.9272 EndY=22.1087 EndZ=0
  constraints (572):
    c: Coincident(g0,g2)
    c: Block(g0)
    c: Block(g1)
    c: Vertical(g3)
    c: Vertical(g4)
    c: Block(g4)
    c: Block(g3)
    c: Tangent(g6,g7) = 1.5708
    c: Tangent(g7,g9) = 1.5708
    c: Equal(g6,g9)
    c: Coincident(g8,g6)
    c: Coincident(g8,g9)
    c: Block(g7)
    c: Block(g8)
    c: Weight(g10) = 1
    c: Equal(g10,g11)
    c: Equal(g10,g12)
    c: InternalAlignment(g10,g13)
    c: InternalAlignment(g11,g13)
    c: InternalAlignment(g12,g13)
    c: InternalAlignment(g14,g13)
    c: InternalAlignment(g15,g13)
    c: Weight(g16) = 1
    c: Equal(g16,g17)
    c: Equal(g16,g18)
    c: InternalAlignment(g16,g19)
    c: InternalAlignment(g17,g19)
    c: InternalAlignment(g18,g19)
    c: InternalAlignment(g20,g19)
    c: InternalAlignment(g21,g19)
    c: Block(g19)
    c: Block(g13)
    c: Weight(g22) = 1
    c: Equal(g22,g23)
    c: Equal(g22,g24)
    c: InternalAlignment(g22,g25)
    c: InternalAlignment(g23,g25)
    c: InternalAlignment(g24,g25)
    c: InternalAlignment(g26,g25)
    c: InternalAlignment(g27,g25)
    c: Weight(g28) = 1
    c: Equal(g28,g29)
    c: Equal(g28,g30)
    c: InternalAlignment(g28,g31)
    c: InternalAlignment(g29,g31)
    c: InternalAlignment(g30,g31)
    c: InternalAlignment(g32,g31)
    c: InternalAlignment(g33,g31)
    c: Block(g31)
    c: Block(g25)
    c: Weight(g34) = 1
    c: Equal(g34,g35)
    c: Equal(g34,g36)
    c: InternalAlignment(g34,g37)
    c: InternalAlignment(g35,g37)
    c: InternalAlignment(g36,g37)
    c: InternalAlignment(g38,g37)
    c: InternalAlignment(g39,g37)
    c: Weight(g40) = 1
    c: Equal(g40,g41)
    c: Equal(g40,g42)
    c: InternalAlignment(g40,g43)
    c: InternalAlignment(g41,g43)
    c: InternalAlignment(g42,g43)
    c: InternalAlignment(g44,g43)
    c: InternalAlignment(g45,g43)
    c: Block(g37)
    c: Block(g43)
    c: Coincident(g46,g4)
    c: Coincident(g46,g3)
    c: Horizontal(g46)
    c: Distance(g46) = 450
    c: Coincident(g47,g4)
    c: Coincident(g47,g3)
    c: Horizontal(g47)
    c: Horizontal(g48)
    c: Coincident(g2,g48)
    c: Block(g48)
    c: Coincident(g1,g48)
    c: Weight(g49) = 1
    c: Equal(g49,g50)
    c: Equal(g49,g51)
    c: InternalAlignment(g49,g52)
    c: InternalAlignment(g50,g52)
    c: InternalAlignment(g51,g52)
    c: InternalAlignment(g53,g52)
    c: InternalAlignment(g54,g52)
    c: Block(g52)
    c: Weight(g55) = 1
    c: Equal(g55,g56)
    c: Equal(g55,g57)
    c: InternalAlignment(g55,g58)
    c: InternalAlignment(g56,g58)
    c: InternalAlignment(g57,g58)
    c: InternalAlignment(g59,g58)
    c: InternalAlignment(g60,g58)
    c: Block(g58)
    c: Weight(g61) = 1
    c: Equal(g61,g62)
    c: Equal(g61,g63)
    c: InternalAlignment(g61,g64)
    c: InternalAlignment(g62,g64)
    c: InternalAlignment(g63,g64)
    c: InternalAlignment(g65,g64)
    c: InternalAlignment(g66,g64)
    c: Block(g64)
    c: Weight(g67) = 1
    c: Equal(g67,g68)
    c: Equal(g67,g69)
    c: InternalAlignment(g67,g70)
    c: InternalAlignment(g68,g70)
    c: InternalAlignment(g69,g70)
    c: InternalAlignment(g71,g70)
    c: InternalAlignment(g72,g70)
    c: Block(g70)
    c: Weight(g73) = 1
    c: Equal(g73,g74)
    c: Equal(g73,g75)
    c: InternalAlignment(g73,g76)
    c: InternalAlignment(g74,g76)
    c: InternalAlignment(g75,g76)
    c: InternalAlignment(g77,g76)
    c: InternalAlignment(g78,g76)
    c: Weight(g79) = 1
    c: Equal(g79,g80)
    c: Equal(g79,g81)
    c: InternalAlignment(g79,g82)
    c: InternalAlignment(g80,g82)
    c: InternalAlignment(g81,g82)
    c: InternalAlignment(g83,g82)
    c: InternalAlignment(g84,g82)
    c: Block(g76)
    c: Block(g82)
    c: Coincident(g85,g76)
    c: Coincident(g85,g82)
    c: Vertical(g85)
    c: Coincident(g86,g76)
    c: Coincident(g86,g58)
    c: Coincident(g87,g58)
    c: Coincident(g87,g82)
    c: Weight(g88) = 1
    c: Equal(g88,g89)
    c: Equal(g88,g90)
    c: InternalAlignment(g88,g91)
    c: InternalAlignment(g89,g91)
    c: InternalAlignment(g90,g91)
    c: InternalAlignment(g92,g91)
    c: InternalAlignment(g93,g91)
    c: Weight(g94) = 1
    c: Equal(g94,g95)
    c: Equal(g94,g96)
    c: InternalAlignment(g94,g97)
    c: InternalAlignment(g95,g97)
    c: InternalAlignment(g96,g97)
    c: InternalAlignment(g98,g97)
    c: InternalAlignment(g99,g97)
    c: Block(g91)
    c: Block(g97)
    c: Coincident(g100,g91)
    c: Coincident(g100,g97)
    c: Vertical(g100)
    c: Coincident(g101,g91)
    c: Coincident(g101,g52)
    c: Coincident(g102,g52)
    c: Coincident(g102,g97)
    c: Weight(g103) = 1
    c: Equal(g103,g104)
    c: Equal(g103,g105)
    c: InternalAlignment(g103,g106)
    c: InternalAlignment(g104,g106)
    c: InternalAlignment(g105,g106)
    c: InternalAlignment(g107,g106)
    c: InternalAlignment(g108,g106)
    c: Weight(g109) = 1
    c: Equal(g109,g110)
    c: Equal(g109,g111)
    c: InternalAlignment(g109,g112)
    c: InternalAlignment(g110,g112)
    c: InternalAlignment(g111,g112)
    c: InternalAlignment(g113,g112)
    c: InternalAlignment(g114,g112)
    c: Block(g106)
    c: Block(g112)
    c: Coincident(g115,g106)
    c: Coincident(g115,g112)
    c: Vertical(g115)
    c: Coincident(g116,g112)
    c: Coincident(g116,g70)
    c: Coincident(g117,g70)
    c: Coincident(g117,g106)
    c: Weight(g118) = 1
    c: Equal(g118,g119)
    c: Equal(g118,g120)
    c: InternalAlignment(g118,g121)
    c: InternalAlignment(g119,g121)
    c: InternalAlignment(g120,g121)
    c: InternalAlignment(g122,g121)
    c: InternalAlignment(g123,g121)
    c: Weight(g124) = 1
    c: Equal(g124,g125)
    c: Equal(g124,g126)
    c: InternalAlignment(g124,g127)
    c: InternalAlignment(g125,g127)
    c: InternalAlignment(g126,g127)
    c: InternalAlignment(g128,g127)
    c: InternalAlignment(g129,g127)
    c: Block(g121)
    c: Block(g127)
    c: Coincident(g130,g121)
    c: Coincident(g130,g127)
    c: Vertical(g130)
    c: Coincident(g131,g127)
    c: Coincident(g131,g64)
    c: Coincident(g132,g64)
    c: Coincident(g132,g121)
    c: Weight(g133) = 1
    c: Equal(g133,g134)
    c: Equal(g133,g135)
    c: InternalAlignment(g133,g136)
    c: InternalAlignment(g134,g136)
    c: InternalAlignment(g135,g136)
    c: InternalAlignment(g137,g136)
    c: InternalAlignment(g138,g136)
    c: Weight(g139) = 1
    c: Equal(g139,g140)
    c: Equal(g139,g141)
    c: InternalAlignment(g139,g142)
    c: InternalAlignment(g140,g142)
    c: InternalAlignment(g141,g142)
    c: InternalAlignment(g143,g142)
    c: InternalAlignment(g144,g142)
    c: Weight(g145) = 1
    c: Equal(g145,g146)
    c: Equal(g145,g147)
    c: InternalAlignment(g145,g148)
    c: InternalAlignment(g146,g148)
    c: InternalAlignment(g147,g148)
    c: InternalAlignment(g149,g148)
    c: InternalAlignment(g150,g148)
    c: Weight(g151) = 1
    c: Equal(g151,g152)
    c: Equal(g151,g153)
    c: InternalAlignment(g151,g154)
    c: InternalAlignment(g152,g154)
    c: InternalAlignment(g153,g154)
    c: InternalAlignment(g155,g154)
    c: InternalAlignment(g156,g154)
    c: Block(g154)
    c: Block(g148)
    c: Block(g142)
    c: Block(g136)
    c: Coincident(g157,g31)
    c: Coincident(g157,g154)
    c: Coincident(g158,g154)
    c: Coincident(g158,g148)
    c: Horizontal(g158)
    c: Coincident(g159,g148)
    c: Coincident(g159,g31)
    c: Vertical(g159)
    c: Coincident(g160,g25)
    c: Coincident(g160,g142)
    c: Vertical(g160)
    c: Coincident(g161,g142)
    c: Coincident(g161,g136)
    c: Horizontal(g161)
    c: Coincident(g162,g136)
    c: Coincident(g162,g25)
    c: Weight(g163) = 1
    c: Equal(g163,g164)
    c: Equal(g163,g165)
    c: InternalAlignment(g163,g166)
    c: InternalAlignment(g164,g166)
    c: InternalAlignment(g165,g166)
    c: InternalAlignment(g167,g166)
    c: InternalAlignment(g168,g166)
    c: Weight(g169) = 1
    c: Equal(g169,g170)
    c: Equal(g169,g171)
    c: InternalAlignment(g169,g172)
    c: InternalAlignment(g170,g172)
    c: InternalAlignment(g171,g172)
    c: InternalAlignment(g173,g172)
    c: InternalAlignment(g174,g172)
    c: Weight(g175) = 1
    c: Equal(g175,g176)
    c: Equal(g175,g177)
    c: InternalAlignment(g175,g178)
    c: InternalAlignment(g176,g178)
    c: InternalAlignment(g177,g178)
    c: InternalAlignment(g179,g178)
    c: InternalAlignment(g180,g178)
    c: Weight(g181) = 1
    c: Equal(g181,g182)
    c: Equal(g181,g183)
    c: InternalAlignment(g181,g184)
    c: InternalAlignment(g182,g184)
    c: InternalAlignment(g183,g184)
    c: InternalAlignment(g185,g184)
    c: InternalAlignment(g186,g184)
    c: Block(g184)
    c: Block(g178)
    c: Block(g172)
    c: Block(g166)
    c: Coincident(g187,g184)
    c: Coincident(g187,g178)
    c: Horizontal(g187)
    c: Coincident(g188,g178)
    c: Coincident(g188,g13)
    c: Vertical(g188)
    c: Coincident(g189,g19)
    c: Coincident(g189,g172)
    c: Vertical(g189)
    c: Coincident(g190,g172)
    c: Coincident(g190,g166)
    c: Horizontal(g190)
    c: Coincident(g191,g166)
    c: Coincident(g191,g19)
    c: Coincident(g192,g13)
    c: Weight(g193) = 1
    c: Equal(g193,g194)
    c: Equal(g193,g195)
    c: InternalAlignment(g193,g196)
    c: InternalAlignment(g194,g196)
    c: InternalAlignment(g195,g196)
    c: InternalAlignment(g197,g196)
    c: InternalAlignment(g198,g196)
    c: Weight(g199) = 1
    c: Equal(g199,g200)
    c: Equal(g199,g201)
    c: InternalAlignment(g199,g202)
    c: InternalAlignment(g200,g202)
    c: InternalAlignment(g201,g202)
    c: InternalAlignment(g203,g202)
    c: InternalAlignment(g204,g202)
    c: Block(g202)
    c: Block(g196)
    c: Coincident(g205,g202)
    c: Coincident(g205,g37)
    c: Coincident(g206,g37)
    c: Coincident(g206,g196)
    c: Coincident(g207,g196)
    c: Coincident(g207,g202)
    c: Vertical(g207)
    c: Weight(g208) = 1
    c: Equal(g208,g209)
    c: Equal(g208,g210)
    c: InternalAlignment(g208,g211)
    c: InternalAlignment(g209,g211)
    c: InternalAlignment(g210,g211)
    c: InternalAlignment(g212,g211)
    c: InternalAlignment(g213,g211)
    c: Weight(g214) = 1
    c: Equal(g214,g215)
    c: Equal(g214,g216)
    c: InternalAlignment(g214,g217)
    c: InternalAlignment(g215,g217)
    c: InternalAlignment(g216,g217)
    c: InternalAlignment(g218,g217)
    c: InternalAlignment(g219,g217)
    c: Block(g217)
    c: Block(g211)
    c: Coincident(g220,g211)
    c: Coincident(g220,g43)
    c: Coincident(g221,g43)
    c: Coincident(g221,g217)
    c: Coincident(g222,g217)
    c: Coincident(g222,g211)
    c: Vertical(g222)
    c: Horizontal(g223)
    c: Block(g223)
    c: Vertical(g224)
    c: Block(g224)
    c: Block(g225)
    c: Weight(g226) = 1
    c: Equal(g226,g227)
    c: Equal(g226,g228)
    c: InternalAlignment(g226,g229)
    c: InternalAlignment(g227,g229)
    c: InternalAlignment(g228,g229)
    c: InternalAlignment(g230,g229)
    c: InternalAlignment(g231,g229)
    c: Weight(g232) = 1
    c: Equal(g232,g233)
    c: Equal(g232,g234)
    c: InternalAlignment(g232,g235)
    c: InternalAlignment(g233,g235)
    c: InternalAlignment(g234,g235)
    c: InternalAlignment(g236,g235)
    c: InternalAlignment(g237,g235)
    c: Weight(g238) = 1
    c: Equal(g238,g239)
    c: Equal(g238,g240)
    c: InternalAlignment(g238,g241)
    c: InternalAlignment(g239,g241)
    c: InternalAlignment(g240,g241)
    c: InternalAlignment(g242,g241)
    c: InternalAlignment(g243,g241)
    c: Weight(g244) = 1
    c: Equal(g244,g245)
    c: Equal(g244,g246)
    c: InternalAlignment(g244,g247)
    c: InternalAlignment(g245,g247)
    c: InternalAlignment(g246,g247)
    c: InternalAlignment(g248,g247)
    c: InternalAlignment(g249,g247)
    c: Block(g229)
    c: Block(g235)
    c: Block(g241)
    c: Block(g247)
    c: Coincident(g250,g235)
    c: Coincident(g250,g229)
    c: Horizontal(g250)
    c: Block(g192)
    c: Weight(g251) = 1
    c: Equal(g251,g252)
    c: Equal(g251,g253)
    c: InternalAlignment(g251,g254)
    c: InternalAlignment(g252,g254)
    c: InternalAlignment(g253,g254)
    c: InternalAlignment(g255,g254)
    c: InternalAlignment(g256,g254)
    c: Weight(g257) = 1
    c: Equal(g257,g258)
    c: Equal(g257,g259)
    c: InternalAlignment(g257,g260)
    c: InternalAlignment(g258,g260)
    c: InternalAlignment(g259,g260)
    c: InternalAlignment(g261,g260)
    c: InternalAlignment(g262,g260)
    c: Block(g254)
    c: Block(g260)
    c: Coincident(g263,g254)
    c: Coincident(g263,g260)
    c: Weight(g264) = 1
    c: Equal(g264,g265)
    c: Equal(g264,g266)
    c: InternalAlignment(g264,g267)
    c: InternalAlignment(g265,g267)
    c: InternalAlignment(g266,g267)
    c: InternalAlignment(g268,g267)
    c: InternalAlignment(g269,g267)
    c: Weight(g270) = 1
    c: Equal(g270,g271)
    c: Equal(g270,g272)
    c: InternalAlignment(g270,g273)
    c: InternalAlignment(g271,g273)
    c: InternalAlignment(g272,g273)
    c: InternalAlignment(g274,g273)
    c: InternalAlignment(g275,g273)
    c: Weight(g276) = 1
    c: Equal(g276,g277)
    c: Equal(g276,g278)
    c: InternalAlignment(g276,g279)
    c: InternalAlignment(g277,g279)
    c: InternalAlignment(g278,g279)
    c: InternalAlignment(g280,g279)
    c: InternalAlignment(g281,g279)
    c: Block(g279)
    c: Block(g273)
    c: Block(g267)
    c: Coincident(g282,g273)
    c: Coincident(g282,g267)
    c: Coincident(g283,g267)
    c: Coincident(g283,g279)
    c: Vertical(g283)
    c: Coincident(g284,g279)
    c: Coincident(g284,g273)
    c: Horizontal(g284)
    c: Weight(g285) = 1
    c: Equal(g285,g286)
    c: InternalAlignment(g285,g287)
    c: InternalAlignment(g286,g287)
    c: InternalAlignment(g288,g287)
    c: InternalAlignment(g289,g287)
    c: Weight(g290) = 1
    c: InternalAlignment(g291,g293)
    c: InternalAlignment(g292,g293)
    c: InternalAlignment(g294,g293)
    c: InternalAlignment(g295,g293)
    c: Weight(g296) = 1
    c: Equal(g296,g297)
    c: Equal(g296,g298)
    c: InternalAlignment(g296,g299)
    c: InternalAlignment(g297,g299)
    c: InternalAlignment(g298,g299)
    c: InternalAlignment(g300,g299)
    c: InternalAlignment(g301,g299)
    c: Equal(g302,g303)
    c: Equal(g302,g304)
    c: InternalAlignment(g302,g305)
    c: InternalAlignment(g303,g305)
    c: InternalAlignment(g304,g305)
    c: InternalAlignment(g306,g305)
    c: InternalAlignment(g307,g305)
    c: Block(g293)
    c: Block(g299)
    c: Block(g305)
    c: Block(g287)
    c: Coincident(g308,g287)
    c: Coincident(g308,g293)
    c: Horizontal(g308)
    c: Coincident(g309,g293)
    c: Coincident(g309,g299)
    c: Vertical(g309)
    c: Coincident(g310,g299)
    c: Coincident(g310,g305)
    c: Horizontal(g310)
    c: Coincident(g311,g305)
    c: Coincident(g311,g287)
    c: Weight(g312) = 1
    c: Equal(g312,g313)
    c: Equal(g312,g314)
    c: InternalAlignment(g312,g315)
    c: InternalAlignment(g313,g315)
    c: InternalAlignment(g314,g315)
    c: InternalAlignment(g316,g315)
    c: InternalAlignment(g317,g315)
    c: Weight(g318) = 1
    c: Equal(g318,g319)
    c: Equal(g318,g320)
    c: InternalAlignment(g318,g321)
    c: InternalAlignment(g319,g321)
    c: InternalAlignment(g320,g321)
    c: InternalAlignment(g322,g321)
    c: InternalAlignment(g323,g321)
    c: Weight(g324) = 1
    c: Equal(g324,g325)
    c: Equal(g324,g326)
    c: InternalAlignment(g324,g327)
    c: InternalAlignment(g325,g327)
    c: InternalAlignment(g326,g327)
    c: InternalAlignment(g328,g327)
    c: InternalAlignment(g329,g327)
    c: Block(g327)
    c: Block(g321)
    c: Block(g315)
    c: Coincident(g330,g327)
    c: Coincident(g330,g321)
    c: Horizontal(g330)
    c: Coincident(g331,g321)
    c: Coincident(g331,g315)
    c: Vertical(g331)
    c: Coincident(g332,g315)
    c: Coincident(g332,g327)
    c: InternalAlignment(g333,g334)
    c: InternalAlignment(g335,g334)
    c: InternalAlignment(g336,g334)
    c: Block(g334)
    c: Equal(g337,g338)
    c: Equal(g337,g339)
    c: InternalAlignment(g337,g340)
    c: InternalAlignment(g338,g340)
    c: InternalAlignment(g339,g340)
    c: InternalAlignment(g341,g340)
    c: InternalAlignment(g342,g340)
    c: Block(g340)
    c: Coincident(g343,g334)
    c: Horizontal(g343)
    c: Block(g343)
    c: Coincident(g344,g334)
    c: Coincident(g344,g260)
    c: Vertical(g344)
    c: Coincident(g345,g340)
    c: Coincident(g345,g254)
    c: Vertical(g345)
    c: Coincident(g347,g5)
    c: Coincident(g348,g5)
    c: Block(g346)
    c: Block(g5)
    c: Block(g348)
    c: Block(g347)
    c: Distance(g344) = 119.89
FEATURE [Sketcher::SketchObject] Sketch001
  FullyConstrained = true
  MapMode = 4
  Placement = pos=(0,0,0) rot=(0.57735,0.57735,0.57735;2.0944rad)
  Support = -> [Sketch]
  sketch-geometry (46):
    g0: BSplineCurve PolesCount=3 KnotsCount=2 Degree=2 IsPeriodic=0
    g1: ArcOfCircle CenterX=73.1223 CenterY=-32.291 CenterZ=0 NormalX=0 NormalY=0 NormalZ=1 AngleXU=0 Radius=13 StartAngle=5.92268 EndAngle=9.06428
    g2: ArcOfCircle CenterX=66.7816 CenterY=-49.1439 CenterZ=0 NormalX=0 NormalY=0 NormalZ=1 AngleXU=0 Radius=13 StartAngle=2.78068 EndAngle=5.92131
    g3: ArcOfCircle CenterX=55.9263 CenterY=-78.1807 CenterZ=0 NormalX=0 NormalY=0 NormalZ=1 AngleXU=0 Radius=13 StartAngle=5.92268 EndAngle=9.06428
    g4: ArcOfCircle CenterX=49.5884 CenterY=-95.0342 CenterZ=0 NormalX=0 NormalY=0 NormalZ=1 AngleXU=0 Radius=13 StartAngle=2.78068 EndAngle=5.92131
    g5: ArcOfCircle CenterX=38.7206 CenterY=-124.067 CenterZ=0 NormalX=0 NormalY=0 NormalZ=1 AngleXU=0 Radius=13 StartAngle=5.92268 EndAngle=9.06428
    g6: ArcOfCircle CenterX=32.3875 CenterY=-140.92 CenterZ=0 NormalX=0 NormalY=0 NormalZ=1 AngleXU=0 Radius=13 StartAngle=2.78068 EndAngle=5.92131
    g7: ArcOfCircle CenterX=21.4715 CenterY=-169.934 CenterZ=0 NormalX=0 NormalY=0 NormalZ=1 AngleXU=0 Radius=13 StartAngle=5.92268 EndAngle=9.06428
    g8: ArcOfCircle CenterX=15.1336 CenterY=-186.787 CenterZ=0 NormalX=0 NormalY=0 NormalZ=1 AngleXU=0 Radius=13 StartAngle=2.78068 EndAngle=5.92131
    g9-g12: Circle x4 (B-spline internal-alignment scaffolding for g13; pole/knot coordinates omitted)
    g13: BSplineCurve PolesCount=4 KnotsCount=2 Degree=3 IsPeriodic=0
    g14: GeomPoint X=28.8094 Y=-19.0875 Z=0
    g15: GeomPoint X=47.0443 Y=-50.4712 Z=0
    g16: Circle CenterX=53.5586 CenterY=-23.2695 CenterZ=0 NormalX=0 NormalY=0 NormalZ=1 AngleXU=0 Radius=3.24518
    g17: Circle CenterX=-195.441 CenterY=-127.082 CenterZ=0 NormalX=0 NormalY=0 NormalZ=1 AngleXU=0 Radius=1
    g18: Circle CenterX=-8.24091 CenterY=-197.481 CenterZ=0 NormalX=0 NormalY=0 NormalZ=1 AngleXU=0 Radius=1
    g19: Circle CenterX=12.8789 CenterY=-141.321 CenterZ=0 NormalX=0 NormalY=0 NormalZ=1 AngleXU=0 Radius=1
    g20: BSplineCurve PolesCount=3 KnotsCount=2 Degree=2 IsPeriodic=0
    g21: GeomPoint X=-195.441 Y=-127.082 Z=0
    g22: GeomPoint X=12.8789 Y=-141.321 Z=0
    g23: Circle CenterX=-12.8016 CenterY=-179.036 CenterZ=0 NormalX=0 NormalY=0 NormalZ=1 AngleXU=0 Radius=10.5072
    g24: Circle CenterX=0.933922 CenterY=-166.43 CenterZ=0 NormalX=0 NormalY=0 NormalZ=1 AngleXU=0 Radius=3.26661
    g25: Circle CenterX=-33.5518 CenterY=-176.44 CenterZ=0 NormalX=0 NormalY=0 NormalZ=1 AngleXU=0 Radius=5.64388
    g26: Circle CenterX=-47.2366 CenterY=-173.859 CenterZ=0 NormalX=0 NormalY=0 NormalZ=1 AngleXU=0 Radius=3.01653
    g27: Circle CenterX=-56.2595 CenterY=-171.456 CenterZ=0 NormalX=0 NormalY=0 NormalZ=1 AngleXU=0 Radius=2.12826
    g28: ArcOfCircle CenterX=51.2151 CenterY=-198.473 CenterZ=0 NormalX=0 NormalY=0 NormalZ=1 AngleXU=0 Radius=20 StartAngle=2.78189 EndAngle=4.35269
    g29: LineSegment StartX=32.4951 StartY=-191.433 StartZ=0 EndX=94.6578 EndY=-26.1352 EndZ=0
    g30: LineSegment StartX=43.1192 StartY=-220.001 StartZ=0 EndX=-196.497 EndY=-129.89 EndZ=0
    g31: LineSegment StartX=43.1192 StartY=-220.001 StartZ=0 EndX=44.1752 EndY=-217.193 EndZ=0
    g32: LineSegment StartX=117.223 StartY=-19.0875 StartZ=0 EndX=117.223 EndY=-16.0875 EndZ=0
    g33: LineSegment StartX=117.223 StartY=-16.0875 StartZ=0 EndX=17.2232 EndY=-16.0875 EndZ=0
    g34: LineSegment StartX=17.2232 StartY=-16.0875 StartZ=0 EndX=17.2232 EndY=-19.0875 EndZ=0
    g35: LineSegment StartX=28.8094 StartY=-19.0875 StartZ=0 EndX=17.2232 EndY=-19.0875 EndZ=0
    g36: LineSegment StartX=47.0443 StartY=-50.4712 StartZ=0 EndX=12.8789 EndY=-141.321 EndZ=0
    g37: LineSegment StartX=-195.441 StartY=-127.082 StartZ=0 EndX=-196.497 EndY=-129.89 EndZ=0
    g38: LineSegment StartX=85.2866 StartY=-36.8766 StartZ=0 EndX=78.9396 EndY=-53.7463 EndZ=0
    g39: LineSegment StartX=60.9579 StartY=-27.7053 StartZ=0 EndX=54.6191 EndY=-44.5532 EndZ=0
    g40: LineSegment StartX=68.0907 StartY=-82.7664 StartZ=0 EndX=61.7465 EndY=-99.6365 EndZ=0
    g41: LineSegment StartX=43.7619 StartY=-73.595 StartZ=0 EndX=37.426 EndY=-90.4435 EndZ=0
    g42: LineSegment StartX=50.885 StartY=-128.652 StartZ=0 EndX=44.5456 EndY=-145.522 EndZ=0
    g43: LineSegment StartX=26.5562 StartY=-119.481 StartZ=0 EndX=20.2251 EndY=-136.329 EndZ=0
    g44: LineSegment StartX=9.3071 StartY=-165.349 StartZ=0 EndX=2.97115 EndY=-182.197 EndZ=0
    g45: LineSegment StartX=33.6358 StartY=-174.52 StartZ=0 EndX=27.2917 EndY=-191.39 EndZ=0
  constraints (71):
    c: Block(g0)
    c: Block(g1)
    c: Block(g2)
    c: Block(g4)
    c: Block(g3)
    c: Block(g6)
    c: Block(g5)
    c: Block(g8)
    c: Block(g7)
    c: Weight(g9) = 1
    c: Equal(g9,g10)
    c: Equal(g9,g11)
    c: Equal(g9,g12)
    c: InternalAlignment(g9-g12 -> g13) x4
    c: InternalAlignment(g14,g13)
    c: InternalAlignment(g15,g13)
    c: Block(g16)
    c: Weight(g17) = 1
    c: Equal(g17,g18)
    c: Equal(g17,g19)
    c: InternalAlignment(g17,g20)
    c: InternalAlignment(g18,g20)
    c: InternalAlignment(g19,g20)
    c: InternalAlignment(g21,g20)
    c: InternalAlignment(g22,g20)
    c: Block(g20)
    c: Block(g23)
    c: Block(g24)
    c: Block(g25)
    c: Block(g26)
    c: Block(g27)
    c: Block(g28)
    c: Coincident(g29,g28)
    c: Coincident(g29,g0)
    c: Block(g13)
    c: Coincident(g31,g30)
    c: Coincident(g31,g28)
    c: Block(g31)
    c: Coincident(g32,g0)
    c: Vertical(g32)
    c: Coincident(g33,g32)
    c: Horizontal(g33)
    c: Coincident(g34,g33)
    c: Vertical(g34)
    c: Block(g33)
    c: Coincident(g35,g13)
    c: Coincident(g35,g34)
    c: Horizontal(g35)
    c: Coincident(g36,g13)
    c: Coincident(g36,g20)
    c: Coincident(g37,g20)
    c: Coincident(g37,g30)
    c: Block(g30)
    c: Coincident(g38,g1)
    c: Coincident(g38,g2)
    c: Coincident(g39,g1)
    c: Coincident(g39,g2)
    c: Coincident(g40,g3)
    c: Coincident(g40,g4)
    c: Coincident(g41,g3)
    c: Coincident(g41,g4)
    c: Coincident(g42,g5)
    c: Coincident(g42,g6)
    c: Coincident(g43,g5)
    c: Coincident(g43,g6)
    c: Coincident(g44,g7)
    c: Coincident(g44,g8)
    c: Coincident(g45,g7)
    c: Coincident(g45,g8)
    c: Distance(g30) = 256
    c: Distance(g33) = 100
FEATURE [Part::Extrusion] Extrude002
  Base = -> Sketch001
  Dir = (1,0,0)
  DirMode = 2
  FaceMakerClass = Part::FaceMakerBullseye
  LengthFwd = 8
  LengthRev = 0
  Solid = true
  Symmetric = false
FEATURE [Sketcher::SketchObject] Sketch002
  FullyConstrained = true
  sketch-geometry (20):
    g0: LineSegment StartX=-2.77179 StartY=-200.304 StartZ=0 EndX=5.22821 EndY=-200.304 EndZ=0
    g1: LineSegment StartX=5.22821 StartY=-200.304 StartZ=0 EndX=5.22821 EndY=-197.304 EndZ=0
    g2: LineSegment StartX=-2.77179 StartY=-200.304 StartZ=0 EndX=-2.77179 EndY=-197.304 EndZ=0
    g3: LineSegment StartX=5.22821 StartY=-197.304 StartZ=0 EndX=8.22821 EndY=-197.304 EndZ=0
    g4: LineSegment StartX=-2.77179 StartY=-197.304 StartZ=0 EndX=-5.77179 EndY=-197.304 EndZ=0
    g5: LineSegment StartX=19.2282 StartY=-203.304 StartZ=0 EndX=19.2282 EndY=-206.304 EndZ=0
    g6: LineSegment StartX=-16.7718 StartY=-203.304 StartZ=0 EndX=-16.7718 EndY=-206.304 EndZ=0
    g7: LineSegment StartX=-16.7718 StartY=-206.304 StartZ=0 EndX=19.2282 EndY=-206.304 EndZ=0
    g8: Circle CenterX=-16.7718 CenterY=-203.304 CenterZ=0 NormalX=0 NormalY=0 NormalZ=1 AngleXU=0 Radius=1
    g9: Circle CenterX=-5.77179 CenterY=-203.304 CenterZ=0 NormalX=0 NormalY=0 NormalZ=1 AngleXU=0 Radius=1
    g10: Circle CenterX=-5.77179 CenterY=-197.304 CenterZ=0 NormalX=0 NormalY=0 NormalZ=1 AngleXU=0 Radius=1
    g11: BSplineCurve PolesCount=3 KnotsCount=2 Degree=2 IsPeriodic=0
    g12: GeomPoint X=-16.7718 Y=-203.304 Z=0
    g13: GeomPoint X=-5.77179 Y=-197.304 Z=0
    g14: Circle CenterX=19.2282 CenterY=-203.304 CenterZ=0 NormalX=0 NormalY=0 NormalZ=1 AngleXU=0 Radius=1
    g15: Circle CenterX=8.22821 CenterY=-203.304 CenterZ=0 NormalX=0 NormalY=0 NormalZ=1 AngleXU=0 Radius=1
    g16: Circle CenterX=8.22821 CenterY=-197.304 CenterZ=0 NormalX=0 NormalY=0 NormalZ=1 AngleXU=0 Radius=1
    g17: BSplineCurve PolesCount=3 KnotsCount=2 Degree=2 IsPeriodic=0
    g18: GeomPoint X=19.2282 Y=-203.304 Z=0
    g19: GeomPoint X=8.22821 Y=-197.304 Z=0
  constraints (41):
    c: Horizontal(g0)
    c: Distance(g0) = 8
    c: Coincident(g1,g0)
    c: Vertical(g1)
    c: Distance(g1) = 3
    c: Coincident(g2,g0)
    c: Vertical(g2)
    c: Distance(g2) = 3
    c: Coincident(g3,g1)
    c: Horizontal(g3)
    c: Distance(g3) = 3
    c: Coincident(g4,g2)
    c: Horizontal(g4)
    c: Distance(g4) = 3
    c: Vertical(g5)
    c: Vertical(g6)
    c: Coincident(g7,g6)
    c: Coincident(g7,g5)
    c: Weight(g8) = 1
    c: Equal(g8,g9)
    c: Equal(g8,g10)
    c: Coincident(g11,g4)
    c: InternalAlignment(g8,g11)
    c: InternalAlignment(g9,g11)
    c: InternalAlignment(g10,g11)
    c: InternalAlignment(g12,g11)
    c: InternalAlignment(g13,g11)
    c: Coincident(g17,g5)
    c: Weight(g14) = 1
    c: Equal(g14,g15)
    c: Equal(g14,g16)
    c: Coincident(g17,g3)
    c: InternalAlignment(g14,g17)
    c: InternalAlignment(g15,g17)
    c: InternalAlignment(g16,g17)
    c: InternalAlignment(g18,g17)
    c: InternalAlignment(g19,g17)
    c: Block(g7)
    c: Block(g17)
    c: Block(g11)
    c: Block(g6)
FEATURE [Part::Extrusion] Extrude003
  Base = -> Sketch002
  Dir = (0,0,1)
  DirMode = 2
  FaceMakerClass = Part::FaceMakerBullseye
  LengthFwd = 260
  LengthRev = 0
  Solid = true
  Symmetric = false
FEATURE [Sketcher::SketchObject] Sketch003
  FullyConstrained = false
  sketch-geometry (382):
    g0: LineSegment StartX=-42.9272 StartY=136.221 StartZ=0 EndX=-42.9272 EndY=-103.779 EndZ=0
    g1: LineSegment StartX=407.073 StartY=136.221 StartZ=0 EndX=407.073 EndY=-103.779 EndZ=0
    g2: ArcOfCircle CenterX=-26.9272 CenterY=-83.7794 CenterZ=0 NormalX=0 NormalY=0 NormalZ=1 AngleXU=0 Radius=8 StartAngle=3.14159 EndAngle=6.28319
    g3: ArcOfCircle CenterX=391.073 CenterY=-83.7794 CenterZ=0 NormalX=0 NormalY=0 NormalZ=1 AngleXU=0 Radius=8 StartAngle=3.14159 EndAngle=6.28319
    g4: Circle CenterX=175.022 CenterY=27.0628 CenterZ=0 NormalX=0 NormalY=0 NormalZ=1 AngleXU=0 Radius=1
    g5: Circle CenterX=179.022 CenterY=24.8665 CenterZ=0 NormalX=0 NormalY=0 NormalZ=1 AngleXU=0 Radius=1
    g6: Circle CenterX=179.022 CenterY=27.0628 CenterZ=0 NormalX=0 NormalY=0 NormalZ=1 AngleXU=0 Radius=1
    g7: BSplineCurve PolesCount=3 KnotsCount=2 Degree=2 IsPeriodic=0
    g8: GeomPoint X=175.022 Y=27.0628 Z=0
    g9: GeomPoint X=179.022 Y=27.0628 Z=0
    g10: Circle CenterX=189.124 CenterY=27.0628 CenterZ=0 NormalX=0 NormalY=0 NormalZ=1 AngleXU=0 Radius=1
    g11: Circle CenterX=185.124 CenterY=24.8665 CenterZ=0 NormalX=0 NormalY=0 NormalZ=1 AngleXU=0 Radius=1
    g12: Circle CenterX=185.124 CenterY=27.0628 CenterZ=0 NormalX=0 NormalY=0 NormalZ=1 AngleXU=0 Radius=1
    g13: BSplineCurve PolesCount=3 KnotsCount=2 Degree=2 IsPeriodic=0
    g14: GeomPoint X=189.124 Y=27.0628 Z=0
    g15: GeomPoint X=185.124 Y=27.0628 Z=0
    g16: Circle CenterX=175.022 CenterY=5.37834 CenterZ=0 NormalX=0 NormalY=0 NormalZ=1 AngleXU=0 Radius=1
    g17: Circle CenterX=179.022 CenterY=7.57463 CenterZ=0 NormalX=0 NormalY=0 NormalZ=1 AngleXU=0 Radius=1
    g18: Circle CenterX=179.022 CenterY=5.34704 CenterZ=0 NormalX=0 NormalY=0 NormalZ=1 AngleXU=0 Radius=1
    g19: BSplineCurve PolesCount=3 KnotsCount=2 Degree=2 IsPeriodic=0
    g20: GeomPoint X=175.022 Y=5.37834 Z=0
    g21: GeomPoint X=179.022 Y=5.34704 Z=0
    g22: Circle CenterX=189.124 CenterY=5.37834 CenterZ=0 NormalX=0 NormalY=0 NormalZ=1 AngleXU=0 Radius=1
    g23: Circle CenterX=185.124 CenterY=7.57463 CenterZ=0 NormalX=0 NormalY=0 NormalZ=1 AngleXU=0 Radius=1
    g24: Circle CenterX=185.124 CenterY=5.34704 CenterZ=0 NormalX=0 NormalY=0 NormalZ=1 AngleXU=0 Radius=1
    g25: BSplineCurve PolesCount=3 KnotsCount=2 Degree=2 IsPeriodic=0
    g26: GeomPoint X=189.124 Y=5.37834 Z=0
    g27: GeomPoint X=185.124 Y=5.34704 Z=0
    g28: Circle CenterX=165.871 CenterY=18.1458 CenterZ=0 NormalX=0 NormalY=0 NormalZ=1 AngleXU=0 Radius=1
    g29: Circle CenterX=169.377 CenterY=16.2206 CenterZ=0 NormalX=0 NormalY=0 NormalZ=1 AngleXU=0 Radius=1
    g30: Circle CenterX=165.871 CenterY=14.2954 CenterZ=0 NormalX=0 NormalY=0 NormalZ=1 AngleXU=0 Radius=1
    g31: BSplineCurve PolesCount=3 KnotsCount=2 Degree=2 IsPeriodic=0
    g32: GeomPoint X=165.871 Y=18.1458 Z=0
    g33: GeomPoint X=165.871 Y=14.2954 Z=0
    g34: Circle CenterX=198.275 CenterY=18.1458 CenterZ=0 NormalX=0 NormalY=0 NormalZ=1 AngleXU=0 Radius=1
    g35: Circle CenterX=194.768 CenterY=16.2206 CenterZ=0 NormalX=0 NormalY=0 NormalZ=1 AngleXU=0 Radius=1
    g36: Circle CenterX=198.275 CenterY=14.2954 CenterZ=0 NormalX=0 NormalY=0 NormalZ=1 AngleXU=0 Radius=1
    g37: BSplineCurve PolesCount=3 KnotsCount=2 Degree=2 IsPeriodic=0
    g38: GeomPoint X=198.275 Y=18.1458 Z=0
    g39: GeomPoint X=198.275 Y=14.2954 Z=0
    g40: LineSegment StartX=407.073 StartY=-103.779 StartZ=0 EndX=-42.9272 EndY=-103.779 EndZ=0
    g41: Circle CenterX=125.607 CenterY=54.1951 CenterZ=0 NormalX=0 NormalY=0 NormalZ=1 AngleXU=0 Radius=1
    g42: Circle CenterX=139.632 CenterY=46.4944 CenterZ=0 NormalX=0 NormalY=0 NormalZ=1 AngleXU=0 Radius=1
    g43: Circle CenterX=127.326 CenterY=56.7187 CenterZ=0 NormalX=0 NormalY=0 NormalZ=1 AngleXU=0 Radius=1
    g44: BSplineCurve PolesCount=3 KnotsCount=2 Degree=2 IsPeriodic=0
    g45: GeomPoint X=125.607 Y=54.1951 Z=0
    g46: GeomPoint X=127.326 Y=56.7187 Z=0
    g47: Circle CenterX=236.821 CenterY=56.7187 CenterZ=0 NormalX=0 NormalY=0 NormalZ=1 AngleXU=0 Radius=1
    g48: Circle CenterX=224.513 CenterY=46.4944 CenterZ=0 NormalX=0 NormalY=0 NormalZ=1 AngleXU=0 Radius=1
    g49: Circle CenterX=238.538 CenterY=54.1951 CenterZ=0 NormalX=0 NormalY=0 NormalZ=1 AngleXU=0 Radius=1
    g50: BSplineCurve PolesCount=3 KnotsCount=2 Degree=2 IsPeriodic=0
    g51: GeomPoint X=236.821 Y=56.7187 Z=0
    g52: GeomPoint X=238.538 Y=54.1951 Z=0
    g53: Circle CenterX=238.538 CenterY=-21.7539 CenterZ=0 NormalX=0 NormalY=0 NormalZ=1 AngleXU=0 Radius=1
    g54: Circle CenterX=224.513 CenterY=-14.0532 CenterZ=0 NormalX=0 NormalY=0 NormalZ=1 AngleXU=0 Radius=1
    g55: Circle CenterX=236.821 CenterY=-24.2775 CenterZ=0 NormalX=0 NormalY=0 NormalZ=1 AngleXU=0 Radius=1
    g56: BSplineCurve PolesCount=3 KnotsCount=2 Degree=2 IsPeriodic=0
    g57: GeomPoint X=238.538 Y=-21.7539 Z=0
    g58: GeomPoint X=236.821 Y=-24.2775 Z=0
    g59: Circle CenterX=125.607 CenterY=-21.7539 CenterZ=0 NormalX=0 NormalY=0 NormalZ=1 AngleXU=0 Radius=1
    g60: Circle CenterX=139.632 CenterY=-14.0532 CenterZ=0 NormalX=0 NormalY=0 NormalZ=1 AngleXU=0 Radius=1
    g61: Circle CenterX=127.325 CenterY=-24.2775 CenterZ=0 NormalX=0 NormalY=0 NormalZ=1 AngleXU=0 Radius=1
    g62: BSplineCurve PolesCount=3 KnotsCount=2 Degree=2 IsPeriodic=0
    g63: GeomPoint X=125.607 Y=-21.7539 Z=0
    g64: GeomPoint X=127.325 Y=-24.2775 Z=0
    g65: Circle CenterX=302.996 CenterY=111.695 CenterZ=0 NormalX=0 NormalY=0 NormalZ=1 AngleXU=0 Radius=1
    g66: Circle CenterX=306.073 CenterY=114.251 CenterZ=0 NormalX=0 NormalY=0 NormalZ=1 AngleXU=0 Radius=1
    g67: Circle CenterX=306.073 CenterY=110.251 CenterZ=0 NormalX=0 NormalY=0 NormalZ=1 AngleXU=0 Radius=1
    g68: BSplineCurve PolesCount=3 KnotsCount=2 Degree=2 IsPeriodic=0
    g69: GeomPoint X=302.996 Y=111.695 Z=0
    g70: GeomPoint X=306.073 Y=110.251 Z=0
    g71: Circle CenterX=306.073 CenterY=95.2763 CenterZ=0 NormalX=0 NormalY=0 NormalZ=1 AngleXU=0 Radius=1
    g72: Circle CenterX=306.073 CenterY=91.2763 CenterZ=0 NormalX=0 NormalY=0 NormalZ=1 AngleXU=0 Radius=1
    g73: Circle CenterX=302.567 CenterY=89.3511 CenterZ=0 NormalX=0 NormalY=0 NormalZ=1 AngleXU=0 Radius=1
    g74: BSplineCurve PolesCount=3 KnotsCount=2 Degree=2 IsPeriodic=0
    g75: GeomPoint X=306.073 Y=95.2763 Z=0
    g76: GeomPoint X=302.567 Y=89.3511 Z=0
    g77: LineSegment StartX=306.073 StartY=110.251 StartZ=0 EndX=306.073 EndY=95.2763 EndZ=0
    g78: LineSegment StartX=302.996 StartY=111.695 StartZ=0 EndX=236.821 EndY=56.7187 EndZ=0
    g79: LineSegment StartX=238.538 StartY=54.1951 StartZ=0 EndX=302.567 EndY=89.3511 EndZ=0
    g80: Circle CenterX=61.1496 CenterY=111.695 CenterZ=0 NormalX=0 NormalY=0 NormalZ=1 AngleXU=0 Radius=1
    g81: Circle CenterX=58.0728 CenterY=114.251 CenterZ=0 NormalX=0 NormalY=0 NormalZ=1 AngleXU=0 Radius=1
    g82: Circle CenterX=58.0728 CenterY=110.251 CenterZ=0 NormalX=0 NormalY=0 NormalZ=1 AngleXU=0 Radius=1
    g83: BSplineCurve PolesCount=3 KnotsCount=2 Degree=2 IsPeriodic=0
    g84: GeomPoint X=61.1496 Y=111.695 Z=0
    g85: GeomPoint X=58.0728 Y=110.251 Z=0
    g86: Circle CenterX=61.5791 CenterY=89.3511 CenterZ=0 NormalX=0 NormalY=0 NormalZ=1 AngleXU=0 Radius=1
    g87: Circle CenterX=58.0728 CenterY=91.2763 CenterZ=0 NormalX=0 NormalY=0 NormalZ=1 AngleXU=0 Radius=1
    g88: Circle CenterX=58.0728 CenterY=95.2763 CenterZ=0 NormalX=0 NormalY=0 NormalZ=1 AngleXU=0 Radius=1
    g89: BSplineCurve PolesCount=3 KnotsCount=2 Degree=2 IsPeriodic=0
    g90: GeomPoint X=61.5791 Y=89.3511 Z=0
    g91: GeomPoint X=58.0728 Y=95.2763 Z=0
    g92: LineSegment StartX=58.0728 StartY=110.251 StartZ=0 EndX=58.0728 EndY=95.2763 EndZ=0
    g93: LineSegment StartX=61.1496 StartY=111.695 StartZ=0 EndX=127.326 EndY=56.7187 EndZ=0
    g94: LineSegment StartX=125.607 StartY=54.1951 StartZ=0 EndX=61.5791 EndY=89.3511 EndZ=0
    g95: Circle CenterX=61.5791 CenterY=-56.9099 CenterZ=0 NormalX=0 NormalY=0 NormalZ=1 AngleXU=0 Radius=1
    g96: Circle CenterX=58.0728 CenterY=-58.8351 CenterZ=0 NormalX=0 NormalY=0 NormalZ=1 AngleXU=0 Radius=1
    g97: Circle CenterX=58.0728 CenterY=-62.8351 CenterZ=0 NormalX=0 NormalY=0 NormalZ=1 AngleXU=0 Radius=1
    g98: BSplineCurve PolesCount=3 KnotsCount=2 Degree=2 IsPeriodic=0
    g99: GeomPoint X=61.5791 Y=-56.9099 Z=0
    g100: GeomPoint X=58.0728 Y=-62.8351 Z=0
    g101: Circle CenterX=58.0728 CenterY=-77.8102 CenterZ=0 NormalX=0 NormalY=0 NormalZ=1 AngleXU=0 Radius=1
    g102: Circle CenterX=58.0728 CenterY=-81.8102 CenterZ=0 NormalX=0 NormalY=0 NormalZ=1 AngleXU=0 Radius=1
    g103: Circle CenterX=61.1496 CenterY=-79.2541 CenterZ=0 NormalX=0 NormalY=0 NormalZ=1 AngleXU=0 Radius=1
    g104: BSplineCurve PolesCount=3 KnotsCount=2 Degree=2 IsPeriodic=0
    g105: GeomPoint X=58.0728 Y=-77.8102 Z=0
    g106: GeomPoint X=61.1496 Y=-79.2541 Z=0
    g107: LineSegment StartX=58.0728 StartY=-62.8351 StartZ=0 EndX=58.0728 EndY=-77.8102 EndZ=0
    g108: LineSegment StartX=61.1496 StartY=-79.2541 StartZ=0 EndX=127.325 EndY=-24.2775 EndZ=0
    g109: LineSegment StartX=125.607 StartY=-21.7539 StartZ=0 EndX=61.5791 EndY=-56.9099 EndZ=0
    g110: Circle CenterX=302.567 CenterY=-56.9099 CenterZ=0 NormalX=0 NormalY=0 NormalZ=1 AngleXU=0 Radius=1
    g111: Circle CenterX=306.073 CenterY=-58.8351 CenterZ=0 NormalX=0 NormalY=0 NormalZ=1 AngleXU=0 Radius=1
    g112: Circle CenterX=306.073 CenterY=-62.8351 CenterZ=0 NormalX=0 NormalY=0 NormalZ=1 AngleXU=0 Radius=1
    g113: BSplineCurve PolesCount=3 KnotsCount=2 Degree=2 IsPeriodic=0
    g114: GeomPoint X=302.567 Y=-56.9099 Z=0
    g115: GeomPoint X=306.073 Y=-62.8351 Z=0
    g116: Circle CenterX=302.996 CenterY=-79.2541 CenterZ=0 NormalX=0 NormalY=0 NormalZ=1 AngleXU=0 Radius=1
    g117: Circle CenterX=306.073 CenterY=-81.8102 CenterZ=0 NormalX=0 NormalY=0 NormalZ=1 AngleXU=0 Radius=1
    g118: Circle CenterX=306.073 CenterY=-77.8102 CenterZ=0 NormalX=0 NormalY=0 NormalZ=1 AngleXU=0 Radius=1
    g119: BSplineCurve PolesCount=3 KnotsCount=2 Degree=2 IsPeriodic=0
    g120: GeomPoint X=302.996 Y=-79.2541 Z=0
    g121: GeomPoint X=306.073 Y=-77.8102 Z=0
    g122: LineSegment StartX=306.073 StartY=-62.8351 StartZ=0 EndX=306.073 EndY=-77.8102 EndZ=0
    g123: LineSegment StartX=302.996 StartY=-79.2541 StartZ=0 EndX=236.821 EndY=-24.2775 EndZ=0
    g124: LineSegment StartX=238.538 StartY=-21.7539 StartZ=0 EndX=302.567 EndY=-56.9099 EndZ=0
    g125: Circle CenterX=61.6457 CenterY=-88.8112 CenterZ=0 NormalX=0 NormalY=0 NormalZ=1 AngleXU=0 Radius=1
    g126: Circle CenterX=58.0728 CenterY=-91.7794 CenterZ=0 NormalX=0 NormalY=0 NormalZ=1 AngleXU=0 Radius=1
    g127: Circle CenterX=63.9135 CenterY=-91.7794 CenterZ=0 NormalX=0 NormalY=0 NormalZ=1 AngleXU=0 Radius=1
    g128: BSplineCurve PolesCount=3 KnotsCount=2 Degree=2 IsPeriodic=0
    g129: GeomPoint X=61.6457 Y=-88.8112 Z=0
    g130: GeomPoint X=63.9135 Y=-91.7794 Z=0
    g131: Circle CenterX=179.022 CenterY=-85.8163 CenterZ=0 NormalX=0 NormalY=0 NormalZ=1 AngleXU=0 Radius=1
    g132: Circle CenterX=179.022 CenterY=-91.7794 CenterZ=0 NormalX=0 NormalY=0 NormalZ=1 AngleXU=0 Radius=1
    g133: Circle CenterX=171.895 CenterY=-91.7794 CenterZ=0 NormalX=0 NormalY=0 NormalZ=1 AngleXU=0 Radius=1
    g134: BSplineCurve PolesCount=3 KnotsCount=2 Degree=2 IsPeriodic=0
    g135: GeomPoint X=179.022 Y=-85.8163 Z=0
    g136: GeomPoint X=171.895 Y=-91.7794 Z=0
    g137: Circle CenterX=185.124 CenterY=-86.2028 CenterZ=0 NormalX=0 NormalY=0 NormalZ=1 AngleXU=0 Radius=1
    g138: Circle CenterX=185.124 CenterY=-91.7794 CenterZ=0 NormalX=0 NormalY=0 NormalZ=1 AngleXU=0 Radius=1
    g139: Circle CenterX=191.747 CenterY=-91.7794 CenterZ=0 NormalX=0 NormalY=0 NormalZ=1 AngleXU=0 Radius=1
    g140: BSplineCurve PolesCount=3 KnotsCount=2 Degree=2 IsPeriodic=0
    g141: GeomPoint X=185.124 Y=-86.2028 Z=0
    g142: GeomPoint X=191.747 Y=-91.7794 Z=0
    g143: Circle CenterX=299.888 CenterY=-86.6413 CenterZ=0 NormalX=0 NormalY=0 NormalZ=1 AngleXU=0 Radius=1
    g144: Circle CenterX=306.073 CenterY=-91.7794 CenterZ=0 NormalX=0 NormalY=0 NormalZ=1 AngleXU=0 Radius=1
    g145: Circle CenterX=298.776 CenterY=-91.7794 CenterZ=0 NormalX=0 NormalY=0 NormalZ=1 AngleXU=0 Radius=1
    g146: BSplineCurve PolesCount=3 KnotsCount=2 Degree=2 IsPeriodic=0
    g147: GeomPoint X=299.888 Y=-86.6413 Z=0
    g148: GeomPoint X=298.776 Y=-91.7794 Z=0
    g149: LineSegment StartX=189.124 StartY=5.37834 StartZ=0 EndX=299.888 EndY=-86.6413 EndZ=0
    g150: LineSegment StartX=298.776 StartY=-91.7794 StartZ=0 EndX=191.747 EndY=-91.7794 EndZ=0
    g151: LineSegment StartX=185.124 StartY=-86.2028 StartZ=0 EndX=185.124 EndY=5.34704 EndZ=0
    g152: LineSegment StartX=179.022 StartY=5.34704 StartZ=0 EndX=179.022 EndY=-85.8163 EndZ=0
    g153: LineSegment StartX=171.895 StartY=-91.7794 StartZ=0 EndX=63.9135 EndY=-91.7794 EndZ=0
    g154: LineSegment StartX=61.6457 StartY=-88.8112 StartZ=0 EndX=175.022 EndY=5.37834 EndZ=0
    g155: Circle CenterX=302.073 CenterY=124.221 CenterZ=0 NormalX=0 NormalY=0 NormalZ=1 AngleXU=0 Radius=1
    g156: Circle CenterX=306.073 CenterY=124.221 CenterZ=0 NormalX=0 NormalY=0 NormalZ=1 AngleXU=0 Radius=1
    g157: Circle CenterX=302.996 CenterY=121.665 CenterZ=0 NormalX=0 NormalY=0 NormalZ=1 AngleXU=0 Radius=1
    g158: BSplineCurve PolesCount=3 KnotsCount=2 Degree=2 IsPeriodic=0
    g159: GeomPoint X=302.073 Y=124.221 Z=0
    g160: GeomPoint X=302.996 Y=121.665 Z=0
    g161: Circle CenterX=189.124 CenterY=124.221 CenterZ=0 NormalX=0 NormalY=0 NormalZ=1 AngleXU=0 Radius=1
    g162: Circle CenterX=185.124 CenterY=124.221 CenterZ=0 NormalX=0 NormalY=0 NormalZ=1 AngleXU=0 Radius=1
    g163: Circle CenterX=185.124 CenterY=120.221 CenterZ=0 NormalX=0 NormalY=0 NormalZ=1 AngleXU=0 Radius=1
    g164: BSplineCurve PolesCount=3 KnotsCount=2 Degree=2 IsPeriodic=0
    g165: GeomPoint X=189.124 Y=124.221 Z=0
    g166: GeomPoint X=185.124 Y=120.221 Z=0
    g167: Circle CenterX=175.022 CenterY=124.221 CenterZ=0 NormalX=0 NormalY=0 NormalZ=1 AngleXU=0 Radius=1
    g168: Circle CenterX=179.022 CenterY=124.221 CenterZ=0 NormalX=0 NormalY=0 NormalZ=1 AngleXU=0 Radius=1
    g169: Circle CenterX=179.022 CenterY=120.221 CenterZ=0 NormalX=0 NormalY=0 NormalZ=1 AngleXU=0 Radius=1
    g170: BSplineCurve PolesCount=3 KnotsCount=2 Degree=2 IsPeriodic=0
    g171: GeomPoint X=175.022 Y=124.221 Z=0
    g172: GeomPoint X=179.022 Y=120.221 Z=0
    g173: Circle CenterX=62.0728 CenterY=124.221 CenterZ=0 NormalX=0 NormalY=0 NormalZ=1 AngleXU=0 Radius=1
    g174: Circle CenterX=58.0728 CenterY=124.221 CenterZ=0 NormalX=0 NormalY=0 NormalZ=1 AngleXU=0 Radius=1
    g175: Circle CenterX=61.1496 CenterY=121.665 CenterZ=0 NormalX=0 NormalY=0 NormalZ=1 AngleXU=0 Radius=1
    g176: BSplineCurve PolesCount=3 KnotsCount=2 Degree=2 IsPeriodic=0
    g177: GeomPoint X=62.0728 Y=124.221 Z=0
    g178: GeomPoint X=61.1496 Y=121.665 Z=0
    g179: LineSegment StartX=62.0728 StartY=124.221 StartZ=0 EndX=175.022 EndY=124.221 EndZ=0
    g180: LineSegment StartX=179.022 StartY=120.221 StartZ=0 EndX=179.022 EndY=27.0628 EndZ=0
    g181: LineSegment StartX=185.124 StartY=27.0628 StartZ=0 EndX=185.124 EndY=120.221 EndZ=0
    g182: LineSegment StartX=302.996 StartY=121.665 StartZ=0 EndX=189.124 EndY=27.0628 EndZ=0
    g183: LineSegment StartX=175.022 StartY=27.0628 StartZ=0 EndX=61.1496 EndY=121.665 EndZ=0
    g184: Circle CenterX=61.5791 CenterY=75.4095 CenterZ=0 NormalX=0 NormalY=0 NormalZ=1 AngleXU=0 Radius=1
    g185: Circle CenterX=58.0728 CenterY=77.3346 CenterZ=0 NormalX=0 NormalY=0 NormalZ=1 AngleXU=0 Radius=1
    g186: Circle CenterX=58.0728 CenterY=73.3346 CenterZ=0 NormalX=0 NormalY=0 NormalZ=1 AngleXU=0 Radius=1
    g187: BSplineCurve PolesCount=3 KnotsCount=2 Degree=2 IsPeriodic=0
    g188: GeomPoint X=61.5791 Y=75.4095 Z=0
    g189: GeomPoint X=58.0728 Y=73.3346 Z=0
    g190: Circle CenterX=58.0728 CenterY=-40.8935 CenterZ=0 NormalX=0 NormalY=0 NormalZ=1 AngleXU=0 Radius=1
    g191: Circle CenterX=58.0728 CenterY=-44.8935 CenterZ=0 NormalX=0 NormalY=0 NormalZ=1 AngleXU=0 Radius=1
    g192: Circle CenterX=61.5791 CenterY=-42.9683 CenterZ=0 NormalX=0 NormalY=0 NormalZ=1 AngleXU=0 Radius=1
    g193: BSplineCurve PolesCount=3 KnotsCount=2 Degree=2 IsPeriodic=0
    g194: GeomPoint X=58.0728 Y=-40.8935 Z=0
    g195: GeomPoint X=61.5791 Y=-42.9683 Z=0
    g196: LineSegment StartX=61.5791 StartY=-42.9683 StartZ=0 EndX=165.871 EndY=14.2954 EndZ=0
    g197: LineSegment StartX=165.871 StartY=18.1458 StartZ=0 EndX=61.5791 EndY=75.4095 EndZ=0
    g198: LineSegment StartX=58.0728 StartY=73.3346 StartZ=0 EndX=58.0728 EndY=-40.8935 EndZ=0
    g199: Circle CenterX=302.567 CenterY=-42.9683 CenterZ=0 NormalX=0 NormalY=0 NormalZ=1 AngleXU=0 Radius=1
    g200: Circle CenterX=306.073 CenterY=-44.8935 CenterZ=0 NormalX=0 NormalY=0 NormalZ=1 AngleXU=0 Radius=1
    g201: Circle CenterX=306.073 CenterY=-40.8935 CenterZ=0 NormalX=0 NormalY=0 NormalZ=1 AngleXU=0 Radius=1
    g202: BSplineCurve PolesCount=3 KnotsCount=2 Degree=2 IsPeriodic=0
    g203: GeomPoint X=302.567 Y=-42.9683 Z=0
    g204: GeomPoint X=306.073 Y=-40.8935 Z=0
    g205: Circle CenterX=306.073 CenterY=73.3346 CenterZ=0 NormalX=0 NormalY=0 NormalZ=1 AngleXU=0 Radius=1
    g206: Circle CenterX=306.073 CenterY=77.3346 CenterZ=0 NormalX=0 NormalY=0 NormalZ=1 AngleXU=0 Radius=1
    g207: Circle CenterX=302.567 CenterY=75.4095 CenterZ=0 NormalX=0 NormalY=0 NormalZ=1 AngleXU=0 Radius=1
    g208: BSplineCurve PolesCount=3 KnotsCount=2 Degree=2 IsPeriodic=0
    g209: GeomPoint X=306.073 Y=73.3346 Z=0
    g210: GeomPoint X=302.567 Y=75.4095 Z=0
    g211: LineSegment StartX=302.567 StartY=-42.9683 StartZ=0 EndX=198.275 EndY=14.2954 EndZ=0
    g212: LineSegment StartX=198.275 StartY=18.1458 StartZ=0 EndX=302.567 EndY=75.4095 EndZ=0
    g213: LineSegment StartX=306.073 StartY=73.3346 StartZ=0 EndX=306.073 EndY=-40.8935 EndZ=0
    g214: LineSegment StartX=322.073 StartY=105.865 StartZ=0 EndX=328.643 EndY=105.865 EndZ=0
    g215: LineSegment StartX=318.073 StartY=120.221 StartZ=0 EndX=318.073 EndY=109.865 EndZ=0
    g216: LineSegment StartX=336.157 StartY=107.779 StartZ=0 EndX=362.567 EndY=122.294 EndZ=0
    g217: Circle CenterX=362.073 CenterY=124.221 CenterZ=0 NormalX=0 NormalY=0 NormalZ=1 AngleXU=0 Radius=1
    g218: Circle CenterX=366.073 CenterY=124.221 CenterZ=0 NormalX=0 NormalY=0 NormalZ=1 AngleXU=0 Radius=1
    g219: Circle CenterX=362.567 CenterY=122.294 CenterZ=0 NormalX=0 NormalY=0 NormalZ=1 AngleXU=0 Radius=1
    g220: BSplineCurve PolesCount=3 KnotsCount=2 Degree=2 IsPeriodic=0
    g221: GeomPoint X=362.073 Y=124.221 Z=0
    g222: GeomPoint X=362.567 Y=122.294 Z=0
    g223: Circle CenterX=322.073 CenterY=124.221 CenterZ=0 NormalX=0 NormalY=0 NormalZ=1 AngleXU=0 Radius=1
    g224: Circle CenterX=318.073 CenterY=124.221 CenterZ=0 NormalX=0 NormalY=0 NormalZ=1 AngleXU=0 Radius=1
    g225: Circle CenterX=318.073 CenterY=120.221 CenterZ=0 NormalX=0 NormalY=0 NormalZ=1 AngleXU=0 Radius=1
    g226: BSplineCurve PolesCount=3 KnotsCount=2 Degree=2 IsPeriodic=0
    g227: GeomPoint X=322.073 Y=124.221 Z=0
    g228: GeomPoint X=318.073 Y=120.221 Z=0
    g229: Circle CenterX=322.073 CenterY=105.865 CenterZ=0 NormalX=0 NormalY=0 NormalZ=1 AngleXU=0 Radius=1
    g230: Circle CenterX=318.073 CenterY=105.865 CenterZ=0 NormalX=0 NormalY=0 NormalZ=1 AngleXU=0 Radius=1
    g231: Circle CenterX=318.073 CenterY=109.865 CenterZ=0 NormalX=0 NormalY=0 NormalZ=1 AngleXU=0 Radius=1
    g232: BSplineCurve PolesCount=3 KnotsCount=2 Degree=2 IsPeriodic=0
    g233: GeomPoint X=322.073 Y=105.865 Z=0
    g234: GeomPoint X=318.073 Y=109.865 Z=0
    g235: Circle CenterX=336.157 CenterY=107.779 CenterZ=0 NormalX=0 NormalY=0 NormalZ=1 AngleXU=0 Radius=1
    g236: Circle CenterX=332.651 CenterY=105.853 CenterZ=0 NormalX=0 NormalY=0 NormalZ=1 AngleXU=0 Radius=1
    g237: Circle CenterX=328.643 CenterY=105.865 CenterZ=0 NormalX=0 NormalY=0 NormalZ=1 AngleXU=0 Radius=1
    g238: BSplineCurve PolesCount=3 KnotsCount=2 Degree=2 IsPeriodic=0
    g239: GeomPoint X=336.157 Y=107.779 Z=0
    g240: GeomPoint X=328.643 Y=105.865 Z=0
    g241: LineSegment StartX=322.073 StartY=124.221 StartZ=0 EndX=362.073 EndY=124.221 EndZ=0
    g242: Circle CenterX=371.567 CenterY=-80.8644 CenterZ=0 NormalX=0 NormalY=0 NormalZ=1 AngleXU=0 Radius=1
    g243: Circle CenterX=375.073 CenterY=-82.7896 CenterZ=0 NormalX=0 NormalY=0 NormalZ=1 AngleXU=0 Radius=1
    g244: Circle CenterX=375.073 CenterY=-78.7896 CenterZ=0 NormalX=0 NormalY=0 NormalZ=1 AngleXU=0 Radius=1
    g245: BSplineCurve PolesCount=3 KnotsCount=2 Degree=2 IsPeriodic=0
    g246: GeomPoint X=371.567 Y=-80.8644 Z=0
    g247: GeomPoint X=375.073 Y=-78.7896 Z=0
    g248: Circle CenterX=321.579 CenterY=-53.4075 CenterZ=0 NormalX=0 NormalY=0 NormalZ=1 AngleXU=0 Radius=1
    g249: Circle CenterX=318.073 CenterY=-51.4823 CenterZ=0 NormalX=0 NormalY=0 NormalZ=1 AngleXU=0 Radius=1
    g250: Circle CenterX=318.073 CenterY=-47.4805 CenterZ=0 NormalX=0 NormalY=0 NormalZ=1 AngleXU=0 Radius=1
    g251: BSplineCurve PolesCount=3 KnotsCount=2 Degree=2 IsPeriodic=0
    g252: GeomPoint X=321.579 Y=-53.4075 Z=0
    g253: GeomPoint X=318.073 Y=-47.4805 Z=0
    g254: LineSegment StartX=371.567 StartY=-80.8644 StartZ=0 EndX=321.579 EndY=-53.4075 EndZ=0
    g255: Circle CenterX=321.579 CenterY=-67.3492 CenterZ=0 NormalX=0 NormalY=0 NormalZ=1 AngleXU=0 Radius=1
    g256: Circle CenterX=318.073 CenterY=-65.424 CenterZ=0 NormalX=0 NormalY=0 NormalZ=1 AngleXU=0 Radius=1
    g257: Circle CenterX=318.073 CenterY=-69.424 CenterZ=0 NormalX=0 NormalY=0 NormalZ=1 AngleXU=0 Radius=1
    g258: BSplineCurve PolesCount=3 KnotsCount=2 Degree=2 IsPeriodic=0
    g259: GeomPoint X=321.579 Y=-67.3492 Z=0
    g260: GeomPoint X=318.073 Y=-69.424 Z=0
    g261: Circle CenterX=362.567 CenterY=-89.8542 CenterZ=0 NormalX=0 NormalY=0 NormalZ=1 AngleXU=0 Radius=1
    g262: Circle CenterX=366.073 CenterY=-91.7794 CenterZ=0 NormalX=0 NormalY=0 NormalZ=1 AngleXU=0 Radius=1
    g263: Circle CenterX=362.073 CenterY=-91.7794 CenterZ=0 NormalX=0 NormalY=0 NormalZ=1 AngleXU=0 Radius=1
    g264: BSplineCurve PolesCount=3 KnotsCount=2 Degree=2 IsPeriodic=0
    g265: GeomPoint X=362.567 Y=-89.8542 Z=0
    g266: GeomPoint X=362.073 Y=-91.7794 Z=0
    g267: Circle CenterX=322.073 CenterY=-91.7794 CenterZ=0 NormalX=0 NormalY=0 NormalZ=1 AngleXU=0 Radius=1
    g268: Circle CenterX=318.073 CenterY=-91.7794 CenterZ=0 NormalX=0 NormalY=0 NormalZ=1 AngleXU=0 Radius=1
    g269: Circle CenterX=318.073 CenterY=-87.7794 CenterZ=0 NormalX=0 NormalY=0 NormalZ=1 AngleXU=0 Radius=1
    g270: BSplineCurve PolesCount=3 KnotsCount=2 Degree=2 IsPeriodic=0
    g271: GeomPoint X=322.073 Y=-91.7794 Z=0
    g272: GeomPoint X=318.073 Y=-87.7794 Z=0
    g273: LineSegment StartX=362.567 StartY=-89.8542 StartZ=0 EndX=321.579 EndY=-67.3492 EndZ=0
    g274: LineSegment StartX=318.073 StartY=-69.424 StartZ=0 EndX=318.073 EndY=-87.7794 EndZ=0
    g275: LineSegment StartX=322.073 StartY=-91.7794 StartZ=0 EndX=362.073 EndY=-91.7794 EndZ=0
    g276: Circle CenterX=2.07281 CenterY=124.221 CenterZ=0 NormalX=0 NormalY=0 NormalZ=1 AngleXU=0 Radius=1
    g277: Circle CenterX=1.57905 CenterY=122.295 CenterZ=0 NormalX=0 NormalY=0 NormalZ=1 AngleXU=0 Radius=1
    g278: BSplineCurve PolesCount=3 KnotsCount=2 Degree=2 IsPeriodic=0
    g279: GeomPoint X=2.07281 Y=124.221 Z=0
    g280: GeomPoint X=1.57905 Y=122.295 Z=0
    g281: Circle CenterX=42.0728 CenterY=124.221 CenterZ=0 NormalX=0 NormalY=0 NormalZ=1 AngleXU=0 Radius=1
    g282: Circle CenterX=46.0728 CenterY=124.221 CenterZ=0 NormalX=0 NormalY=0 NormalZ=1 AngleXU=0 Radius=1
    g283: Circle CenterX=46.0728 CenterY=120.221 CenterZ=0 NormalX=0 NormalY=0 NormalZ=1 AngleXU=0 Radius=1
    g284: BSplineCurve PolesCount=3 KnotsCount=2 Degree=2 IsPeriodic=0
    g285: GeomPoint X=42.0728 Y=124.221 Z=0
    g286: GeomPoint X=46.0728 Y=120.221 Z=0
    g287: Circle CenterX=46.0728 CenterY=109.865 CenterZ=0 NormalX=0 NormalY=0 NormalZ=1 AngleXU=0 Radius=1
    g288: Circle CenterX=46.0728 CenterY=105.865 CenterZ=0 NormalX=0 NormalY=0 NormalZ=1 AngleXU=0 Radius=1
    g289: Circle CenterX=42.0728 CenterY=105.865 CenterZ=0 NormalX=0 NormalY=0 NormalZ=1 AngleXU=0 Radius=1
    g290: BSplineCurve PolesCount=3 KnotsCount=2 Degree=2 IsPeriodic=0
    g291: GeomPoint X=46.0728 Y=109.865 Z=0
    g292: GeomPoint X=42.0728 Y=105.865 Z=0
    g293: Circle CenterX=35.5028 CenterY=105.865 CenterZ=0 NormalX=0 NormalY=0 NormalZ=1 AngleXU=0 Radius=1
    g294: Circle CenterX=31.5028 CenterY=105.865 CenterZ=0 NormalX=0 NormalY=0 NormalZ=1 AngleXU=0 Radius=1
    g295: Circle CenterX=27.9965 CenterY=107.79 CenterZ=0 NormalX=0 NormalY=0 NormalZ=1 AngleXU=0 Radius=1
    g296: BSplineCurve PolesCount=3 KnotsCount=2 Degree=2 IsPeriodic=0
    g297: GeomPoint X=35.5028 Y=105.865 Z=0
    g298: GeomPoint X=27.9965 Y=107.79 Z=0
    g299: LineSegment StartX=2.07281 StartY=124.221 StartZ=0 EndX=42.0728 EndY=124.221 EndZ=0
    g300: LineSegment StartX=46.0728 StartY=120.221 StartZ=0 EndX=46.0728 EndY=109.865 EndZ=0
    g301: LineSegment StartX=42.0728 StartY=105.865 StartZ=0 EndX=35.5028 EndY=105.865 EndZ=0
    g302: LineSegment StartX=27.9965 StartY=107.79 StartZ=0 EndX=1.57905 EndY=122.295 EndZ=0
    g303: Circle CenterX=42.5666 CenterY=-67.3492 CenterZ=0 NormalX=0 NormalY=0 NormalZ=1 AngleXU=0 Radius=1
    g304: Circle CenterX=46.0728 CenterY=-65.424 CenterZ=0 NormalX=0 NormalY=0 NormalZ=1 AngleXU=0 Radius=1
    g305: Circle CenterX=46.0728 CenterY=-69.424 CenterZ=0 NormalX=0 NormalY=0 NormalZ=1 AngleXU=0 Radius=1
    g306: BSplineCurve PolesCount=3 KnotsCount=2 Degree=2 IsPeriodic=0
    g307: GeomPoint X=42.5666 Y=-67.3492 Z=0
    g308: GeomPoint X=46.0728 Y=-69.424 Z=0
    g309: Circle CenterX=46.0728 CenterY=-87.7794 CenterZ=0 NormalX=0 NormalY=0 NormalZ=1 AngleXU=0 Radius=1
    g310: Circle CenterX=46.0728 CenterY=-91.7794 CenterZ=0 NormalX=0 NormalY=0 NormalZ=1 AngleXU=0 Radius=1
    g311: Circle CenterX=42.0728 CenterY=-91.7794 CenterZ=0 NormalX=0 NormalY=0 NormalZ=1 AngleXU=0 Radius=1
    g312: BSplineCurve PolesCount=3 KnotsCount=2 Degree=2 IsPeriodic=0
    g313: GeomPoint X=46.0728 Y=-87.7794 Z=0
    g314: GeomPoint X=42.0728 Y=-91.7794 Z=0
    g315: Circle CenterX=2.07281 CenterY=-91.7794 CenterZ=0 NormalX=0 NormalY=0 NormalZ=1 AngleXU=0 Radius=1
    g316: Circle CenterX=-1.92719 CenterY=-91.7794 CenterZ=0 NormalX=0 NormalY=0 NormalZ=1 AngleXU=0 Radius=1
    g317: Circle CenterX=1.57905 CenterY=-89.8542 CenterZ=0 NormalX=0 NormalY=0 NormalZ=1 AngleXU=0 Radius=1
    g318: BSplineCurve PolesCount=3 KnotsCount=2 Degree=2 IsPeriodic=0
    g319: GeomPoint X=2.07281 Y=-91.7794 Z=0
    g320: GeomPoint X=1.57905 Y=-89.8542 Z=0
    g321: LineSegment StartX=2.07281 StartY=-91.7794 StartZ=0 EndX=42.0728 EndY=-91.7794 EndZ=0
    g322: LineSegment StartX=46.0728 StartY=-87.7794 StartZ=0 EndX=46.0728 EndY=-69.424 EndZ=0
    g323: LineSegment StartX=42.5666 StartY=-67.3492 StartZ=0 EndX=1.57905 EndY=-89.8542 EndZ=0
    g324: Circle CenterX=322.073 CenterY=76.4095 CenterZ=0 NormalX=0 NormalY=0 NormalZ=1 AngleXU=0 Radius=4
    g325: BSplineCurve PolesCount=3 KnotsCount=2 Degree=2 IsPeriodic=0
    g326: GeomPoint X=318.073 Y=72.4095 Z=0
    g327: GeomPoint X=322.073 Y=76.4095 Z=0
    g328: Circle CenterX=375.073 CenterY=72.4095 CenterZ=0 NormalX=0 NormalY=0 NormalZ=1 AngleXU=0 Radius=1
    g329: Circle CenterX=375.073 CenterY=76.4095 CenterZ=0 NormalX=0 NormalY=0 NormalZ=1 AngleXU=0 Radius=1
    g330: Circle CenterX=371.073 CenterY=76.4095 CenterZ=0 NormalX=0 NormalY=0 NormalZ=1 AngleXU=0 Radius=1
    g331: BSplineCurve PolesCount=3 KnotsCount=2 Degree=2 IsPeriodic=0
    g332: GeomPoint X=375.073 Y=72.4095 Z=0
    g333: GeomPoint X=371.073 Y=76.4095 Z=0
    g334: LineSegment StartX=322.073 StartY=76.4095 StartZ=0 EndX=371.073 EndY=76.4095 EndZ=0
    g335: LineSegment StartX=318.073 StartY=72.4095 StartZ=0 EndX=318.073 EndY=-47.4805 EndZ=0
    g336: LineSegment StartX=375.073 StartY=72.4095 StartZ=0 EndX=375.073 EndY=-78.7896 EndZ=0
    g337: ArcOfCircle CenterX=-26.9272 CenterY=22.1087 CenterZ=0 NormalX=0 NormalY=0 NormalZ=1 AngleXU=0 Radius=4 StartAngle=5e-16 EndAngle=3.14159
    g338: LineSegment StartX=-22.9272 StartY=22.1087 StartZ=0 EndX=-18.9272 EndY=-83.7794 EndZ=0
    g339: LineSegment StartX=-34.9272 StartY=-83.7794 StartZ=0 EndX=-30.9272 EndY=22.1087 EndZ=0
    g340: ArcOfCircle CenterX=391.073 CenterY=22.1087 CenterZ=0 NormalX=0 NormalY=0 NormalZ=1 AngleXU=0 Radius=4 StartAngle=0 EndAngle=3.14159
    g341: LineSegment StartX=387.073 StartY=22.1087 StartZ=0 EndX=383.073 EndY=-83.7794 EndZ=0
    g342: LineSegment StartX=395.073 StartY=22.1087 StartZ=0 EndX=399.073 EndY=-83.7794 EndZ=0
    g343: Circle CenterX=-10.9272 CenterY=-78.7794 CenterZ=0 NormalX=0 NormalY=0 NormalZ=1 AngleXU=0 Radius=1
    g344: Circle CenterX=-10.9272 CenterY=-82.7794 CenterZ=0 NormalX=0 NormalY=0 NormalZ=1 AngleXU=0 Radius=1
    g345: Circle CenterX=-7.42095 CenterY=-80.8542 CenterZ=0 NormalX=0 NormalY=0 NormalZ=1 AngleXU=0 Radius=1
    g346: BSplineCurve PolesCount=3 KnotsCount=2 Degree=2 IsPeriodic=0
    g347: GeomPoint X=-10.9272 Y=-78.7794 Z=0
    g348: GeomPoint X=-7.42095 Y=-80.8542 Z=0
    g349: Circle CenterX=42.5666 CenterY=-53.4075 CenterZ=0 NormalX=0 NormalY=0 NormalZ=1 AngleXU=0 Radius=1
    g350: Circle CenterX=46.0728 CenterY=-51.4823 CenterZ=0 NormalX=0 NormalY=0 NormalZ=1 AngleXU=0 Radius=1
    g351: Circle CenterX=46.0728 CenterY=-47.4823 CenterZ=0 NormalX=0 NormalY=0 NormalZ=1 AngleXU=0 Radius=1
    g352: BSplineCurve PolesCount=3 KnotsCount=2 Degree=2 IsPeriodic=0
    g353: GeomPoint X=42.5666 Y=-53.4075 Z=0
    g354: GeomPoint X=46.0728 Y=-47.4823 Z=0
    g355: Circle CenterX=46.0728 CenterY=72.4095 CenterZ=0 NormalX=0 NormalY=0 NormalZ=1 AngleXU=0 Radius=1
    g356: Circle CenterX=46.0728 CenterY=76.4095 CenterZ=0 NormalX=0 NormalY=0 NormalZ=1 AngleXU=0 Radius=1
    g357: Circle CenterX=42.0728 CenterY=76.4095 CenterZ=0 NormalX=0 NormalY=0 NormalZ=1 AngleXU=0 Radius=1
    g358: BSplineCurve PolesCount=3 KnotsCount=2 Degree=2 IsPeriodic=0
    g359: GeomPoint X=46.0728 Y=72.4095 Z=0
    g360: GeomPoint X=42.0728 Y=76.4095 Z=0
    g361: Circle CenterX=-6.92718 CenterY=76.4095 CenterZ=0 NormalX=0 NormalY=0 NormalZ=1 AngleXU=0 Radius=1
    g362: Circle CenterX=-10.9272 CenterY=76.4095 CenterZ=0 NormalX=0 NormalY=0 NormalZ=1 AngleXU=0 Radius=1
    g363: Circle CenterX=-10.9272 CenterY=72.4095 CenterZ=0 NormalX=0 NormalY=0 NormalZ=1 AngleXU=0 Radius=1
    g364: BSplineCurve PolesCount=3 KnotsCount=2 Degree=2 IsPeriodic=0
    g365: GeomPoint X=-6.92718 Y=76.4095 Z=0
    g366: GeomPoint X=-10.9272 Y=72.4095 Z=0
    g367: LineSegment StartX=-10.9272 StartY=72.4095 StartZ=0 EndX=-10.9272 EndY=-78.7794 EndZ=0
    g368: LineSegment StartX=-7.42095 StartY=-80.8542 StartZ=0 EndX=42.5666 EndY=-53.4075 EndZ=0
    g369: LineSegment StartX=46.0728 StartY=-47.4823 StartZ=0 EndX=46.0728 EndY=72.4095 EndZ=0
    g370: LineSegment StartX=42.0728 StartY=76.4095 StartZ=0 EndX=-6.92719 EndY=76.4095 EndZ=0
    g371: LineSegment StartX=232.072 StartY=136.221 StartZ=0 EndX=232.072 EndY=-117.815 EndZ=0
    g372: LineSegment StartX=132.072 StartY=136.221 StartZ=0 EndX=132.072 EndY=-121.309 EndZ=0
    g373: LineSegment StartX=245.072 StartY=136.221 StartZ=0 EndX=245.072 EndY=-116.499 EndZ=0
    g374: LineSegment StartX=119.072 StartY=136.221 StartZ=0 EndX=119.072 EndY=-116.228 EndZ=0
    g375: LineSegment StartX=-42.9272 StartY=136.221 StartZ=0 EndX=407.073 EndY=136.221 EndZ=0
    g376: LineSegment StartX=232.072 StartY=136.221 StartZ=0 EndX=220.072 EndY=136.221 EndZ=0
    g377: LineSegment StartX=232.072 StartY=136.221 StartZ=0 EndX=232.072 EndY=124.221 EndZ=0
    g378: LineSegment StartX=220.072 StartY=136.221 StartZ=0 EndX=220.072 EndY=124.221 EndZ=0
    g379: LineSegment StartX=220.072 StartY=136.221 StartZ=0 EndX=226.072 EndY=136.221 EndZ=0
    g380: LineSegment StartX=220.072 StartY=136.221 StartZ=0 EndX=220.072 EndY=130.221 EndZ=0
    g381: LineSegment StartX=220.072 StartY=124.221 StartZ=0 EndX=226.072 EndY=124.221 EndZ=0
  constraints (638):
    c: Vertical(g0)
    c: Vertical(g1)
    c: Block(g1)
    c: Block(g0)
    c: Weight(g4) = 1
    c: Equal(g4,g5)
    c: Equal(g4,g6)
    c: InternalAlignment(g4,g7)
    c: InternalAlignment(g5,g7)
    c: InternalAlignment(g6,g7)
    c: InternalAlignment(g8,g7)
    c: InternalAlignment(g9,g7)
    c: Weight(g10) = 1
    c: Equal(g10,g11)
    c: Equal(g10,g12)
    c: InternalAlignment(g10,g13)
    c: InternalAlignment(g11,g13)
    c: InternalAlignment(g12,g13)
    c: InternalAlignment(g14,g13)
    c: InternalAlignment(g15,g13)
    c: Block(g13)
    c: Block(g7)
    c: Weight(g16) = 1
    c: Equal(g16,g17)
    c: Equal(g16,g18)
    c: InternalAlignment(g16,g19)
    c: InternalAlignment(g17,g19)
    c: InternalAlignment(g18,g19)
    c: InternalAlignment(g20,g19)
    c: InternalAlignment(g21,g19)
    c: Weight(g22) = 1
    c: Equal(g22,g23)
    c: Equal(g22,g24)
    c: InternalAlignment(g22,g25)
    c: InternalAlignment(g23,g25)
    c: InternalAlignment(g24,g25)
    c: InternalAlignment(g26,g25)
    c: InternalAlignment(g27,g25)
    c: Block(g25)
    c: Block(g19)
    c: Weight(g28) = 1
    c: Equal(g28,g29)
    c: Equal(g28,g30)
    c: InternalAlignment(g28,g31)
    c: InternalAlignment(g29,g31)
    c: InternalAlignment(g30,g31)
    c: InternalAlignment(g32,g31)
    c: InternalAlignment(g33,g31)
    c: Weight(g34) = 1
    c: Equal(g34,g35)
    c: Equal(g34,g36)
    c: InternalAlignment(g34,g37)
    c: InternalAlignment(g35,g37)
    c: InternalAlignment(g36,g37)
    c: InternalAlignment(g38,g37)
    c: InternalAlignment(g39,g37)
    c: Block(g31)
    c: Block(g37)
    c: Coincident(g40,g1)
    c: Coincident(g40,g0)
    c: Horizontal(g40)
    c: Distance(g40) = 450
    c: Weight(g41) = 1
    c: Equal(g41,g42)
    c: Equal(g41,g43)
    c: InternalAlignment(g41,g44)
    c: InternalAlignment(g42,g44)
    c: InternalAlignment(g43,g44)
    c: InternalAlignment(g45,g44)
    c: InternalAlignment(g46,g44)
    c: Block(g44)
    c: Weight(g47) = 1
    c: Equal(g47,g48)
    c: Equal(g47,g49)
    c: InternalAlignment(g47,g50)
    c: InternalAlignment(g48,g50)
    c: InternalAlignment(g49,g50)
    c: InternalAlignment(g51,g50)
    c: InternalAlignment(g52,g50)
    c: Block(g50)
    c: Weight(g53) = 1
    c: Equal(g53,g54)
    c: Equal(g53,g55)
    c: InternalAlignment(g53,g56)
    c: InternalAlignment(g54,g56)
    c: InternalAlignment(g55,g56)
    c: InternalAlignment(g57,g56)
    c: InternalAlignment(g58,g56)
    c: Block(g56)
    c: Weight(g59) = 1
    c: Equal(g59,g60)
    c: Equal(g59,g61)
    c: InternalAlignment(g59,g62)
    c: InternalAlignment(g60,g62)
    c: InternalAlignment(g61,g62)
    c: InternalAlignment(g63,g62)
    c: InternalAlignment(g64,g62)
    c: Block(g62)
    c: Weight(g65) = 1
    c: Equal(g65,g66)
    c: Equal(g65,g67)
    c: InternalAlignment(g65,g68)
    c: InternalAlignment(g66,g68)
    c: InternalAlignment(g67,g68)
    c: InternalAlignment(g69,g68)
    c: InternalAlignment(g70,g68)
    c: Weight(g71) = 1
    c: Equal(g71,g72)
    c: Equal(g71,g73)
    c: InternalAlignment(g71,g74)
    c: InternalAlignment(g72,g74)
    c: InternalAlignment(g73,g74)
    c: InternalAlignment(g75,g74)
    c: InternalAlignment(g76,g74)
    c: Block(g68)
    c: Block(g74)
    c: Coincident(g77,g68)
    c: Coincident(g77,g74)
    c: Vertical(g77)
    c: Coincident(g78,g68)
    c: Coincident(g78,g50)
    c: Coincident(g79,g50)
    c: Coincident(g79,g74)
    c: Weight(g80) = 1
    c: Equal(g80,g81)
    c: Equal(g80,g82)
    c: InternalAlignment(g80,g83)
    c: InternalAlignment(g81,g83)
    c: InternalAlignment(g82,g83)
    c: InternalAlignment(g84,g83)
    c: InternalAlignment(g85,g83)
    c: Weight(g86) = 1
    c: Equal(g86,g87)
    c: Equal(g86,g88)
    c: InternalAlignment(g86,g89)
    c: InternalAlignment(g87,g89)
    c: InternalAlignment(g88,g89)
    c: InternalAlignment(g90,g89)
    c: InternalAlignment(g91,g89)
    c: Block(g83)
    c: Block(g89)
    c: Coincident(g92,g83)
    c: Coincident(g92,g89)
    c: Vertical(g92)
    c: Coincident(g93,g83)
    c: Coincident(g93,g44)
    c: Coincident(g94,g44)
    c: Coincident(g94,g89)
    c: Weight(g95) = 1
    c: Equal(g95,g96)
    c: Equal(g95,g97)
    c: InternalAlignment(g95,g98)
    c: InternalAlignment(g96,g98)
    c: InternalAlignment(g97,g98)
    c: InternalAlignment(g99,g98)
    c: InternalAlignment(g100,g98)
    c: Weight(g101) = 1
    c: Equal(g101,g102)
    c: Equal(g101,g103)
    c: InternalAlignment(g101,g104)
    c: InternalAlignment(g102,g104)
    c: InternalAlignment(g103,g104)
    c: InternalAlignment(g105,g104)
    c: InternalAlignment(g106,g104)
    c: Block(g98)
    c: Block(g104)
    c: Coincident(g107,g98)
    c: Coincident(g107,g104)
    c: Vertical(g107)
    c: Coincident(g108,g104)
    c: Coincident(g108,g62)
    c: Coincident(g109,g62)
    c: Coincident(g109,g98)
    c: Weight(g110) = 1
    c: Equal(g110,g111)
    c: Equal(g110,g112)
    c: InternalAlignment(g110,g113)
    c: InternalAlignment(g111,g113)
    c: InternalAlignment(g112,g113)
    c: InternalAlignment(g114,g113)
    c: InternalAlignment(g115,g113)
    c: Weight(g116) = 1
    c: Equal(g116,g117)
    c: Equal(g116,g118)
    c: InternalAlignment(g116,g119)
    c: InternalAlignment(g117,g119)
    c: InternalAlignment(g118,g119)
    c: InternalAlignment(g120,g119)
    c: InternalAlignment(g121,g119)
    c: Block(g113)
    c: Block(g119)
    c: Coincident(g122,g113)
    c: Coincident(g122,g119)
    c: Vertical(g122)
    c: Coincident(g123,g119)
    c: Coincident(g123,g56)
    c: Coincident(g124,g56)
    c: Coincident(g124,g113)
    c: Weight(g125) = 1
    c: Equal(g125,g126)
    c: Equal(g125,g127)
    c: InternalAlignment(g125,g128)
    c: InternalAlignment(g126,g128)
    c: InternalAlignment(g127,g128)
    c: InternalAlignment(g129,g128)
    c: InternalAlignment(g130,g128)
    c: Weight(g131) = 1
    c: Equal(g131,g132)
    c: Equal(g131,g133)
    c: InternalAlignment(g131,g134)
    c: InternalAlignment(g132,g134)
    c: InternalAlignment(g133,g134)
    c: InternalAlignment(g135,g134)
    c: InternalAlignment(g136,g134)
    c: Weight(g137) = 1
    c: Equal(g137,g138)
    c: Equal(g137,g139)
    c: InternalAlignment(g137,g140)
    c: InternalAlignment(g138,g140)
    c: InternalAlignment(g139,g140)
    c: InternalAlignment(g141,g140)
    c: InternalAlignment(g142,g140)
    c: Weight(g143) = 1
    c: Equal(g143,g144)
    c: Equal(g143,g145)
    c: InternalAlignment(g143,g146)
    c: InternalAlignment(g144,g146)
    c: InternalAlignment(g145,g146)
    c: InternalAlignment(g147,g146)
    c: InternalAlignment(g148,g146)
    c: Block(g146)
    c: Block(g140)
    c: Block(g134)
    c: Block(g128)
    c: Coincident(g149,g25)
    c: Coincident(g149,g146)
    c: Coincident(g150,g146)
    c: Coincident(g150,g140)
    c: Horizontal(g150)
    c: Coincident(g151,g140)
    c: Coincident(g151,g25)
    c: Vertical(g151)
    c: Coincident(g152,g19)
    c: Coincident(g152,g134)
    c: Vertical(g152)
    c: Coincident(g153,g134)
    c: Coincident(g153,g128)
    c: Horizontal(g153)
    c: Coincident(g154,g128)
    c: Coincident(g154,g19)
    c: Weight(g155) = 1
    c: Equal(g155,g156)
    c: Equal(g155,g157)
    c: InternalAlignment(g155,g158)
    c: InternalAlignment(g156,g158)
    c: InternalAlignment(g157,g158)
    c: InternalAlignment(g159,g158)
    c: InternalAlignment(g160,g158)
    c: Weight(g161) = 1
    c: Equal(g161,g162)
    c: Equal(g161,g163)
    c: InternalAlignment(g161,g164)
    c: InternalAlignment(g162,g164)
    c: InternalAlignment(g163,g164)
    c: InternalAlignment(g165,g164)
    c: InternalAlignment(g166,g164)
    c: Weight(g167) = 1
    c: Equal(g167,g168)
    c: Equal(g167,g169)
    c: InternalAlignment(g167,g170)
    c: InternalAlignment(g168,g170)
    c: InternalAlignment(g169,g170)
    c: InternalAlignment(g171,g170)
    c: InternalAlignment(g172,g170)
    c: Weight(g173) = 1
    c: Equal(g173,g174)
    c: Equal(g173,g175)
    c: InternalAlignment(g173,g176)
    c: InternalAlignment(g174,g176)
    c: InternalAlignment(g175,g176)
    c: InternalAlignment(g177,g176)
    c: InternalAlignment(g178,g176)
    c: Block(g176)
    c: Block(g170)
    c: Block(g164)
    c: Block(g158)
    c: Coincident(g179,g176)
    c: Coincident(g179,g170)
    c: Horizontal(g179)
    c: Coincident(g180,g170)
    c: Coincident(g180,g7)
    c: Vertical(g180)
    c: Coincident(g181,g13)
    c: Coincident(g181,g164)
    c: Vertical(g181)
    c: Coincident(g182,g158)
    c: Coincident(g182,g13)
    c: Coincident(g183,g7)
    c: Weight(g184) = 1
    c: Equal(g184,g185)
    c: Equal(g184,g186)
    c: InternalAlignment(g184,g187)
    c: InternalAlignment(g185,g187)
    c: InternalAlignment(g186,g187)
    c: InternalAlignment(g188,g187)
    c: InternalAlignment(g189,g187)
    c: Weight(g190) = 1
    c: Equal(g190,g191)
    c: Equal(g190,g192)
    c: InternalAlignment(g190,g193)
    c: InternalAlignment(g191,g193)
    c: InternalAlignment(g192,g193)
    c: InternalAlignment(g194,g193)
    c: InternalAlignment(g195,g193)
    c: Block(g193)
    c: Block(g187)
    c: Coincident(g196,g193)
    c: Coincident(g196,g31)
    c: Coincident(g197,g31)
    c: Coincident(g197,g187)
    c: Coincident(g198,g187)
    c: Coincident(g198,g193)
    c: Vertical(g198)
    c: Weight(g199) = 1
    c: Equal(g199,g200)
    c: Equal(g199,g201)
    c: InternalAlignment(g199,g202)
    c: InternalAlignment(g200,g202)
    c: InternalAlignment(g201,g202)
    c: InternalAlignment(g203,g202)
    c: InternalAlignment(g204,g202)
    c: Weight(g205) = 1
    c: Equal(g205,g206)
    c: Equal(g205,g207)
    c: InternalAlignment(g205,g208)
    c: InternalAlignment(g206,g208)
    c: InternalAlignment(g207,g208)
    c: InternalAlignment(g209,g208)
    c: InternalAlignment(g210,g208)
    c: Block(g208)
    c: Block(g202)
    c: Coincident(g211,g202)
    c: Coincident(g211,g37)
    c: Coincident(g212,g37)
    c: Coincident(g212,g208)
    c: Coincident(g213,g208)
    c: Coincident(g213,g202)
    c: Vertical(g213)
    c: Horizontal(g214)
    c: Block(g214)
    c: Vertical(g215)
    c: Block(g215)
    c: Block(g216)
    c: Weight(g217) = 1
    c: Equal(g217,g218)
    c: Equal(g217,g219)
    c: InternalAlignment(g217,g220)
    c: InternalAlignment(g218,g220)
    c: InternalAlignment(g219,g220)
    c: InternalAlignment(g221,g220)
    c: InternalAlignment(g222,g220)
    c: Weight(g223) = 1
    c: Equal(g223,g224)
    c: Equal(g223,g225)
    c: InternalAlignment(g223,g226)
    c: InternalAlignment(g224,g226)
    c: InternalAlignment(g225,g226)
    c: InternalAlignment(g227,g226)
    c: InternalAlignment(g228,g226)
    c: Weight(g229) = 1
    c: Equal(g229,g230)
    c: Equal(g229,g231)
    c: InternalAlignment(g229,g232)
    c: InternalAlignment(g230,g232)
    c: InternalAlignment(g231,g232)
    c: InternalAlignment(g233,g232)
    c: InternalAlignment(g234,g232)
    c: Weight(g235) = 1
    c: Equal(g235,g236)
    c: Equal(g235,g237)
    c: InternalAlignment(g235,g238)
    c: InternalAlignment(g236,g238)
    c: InternalAlignment(g237,g238)
    c: InternalAlignment(g239,g238)
    c: InternalAlignment(g240,g238)
    c: Block(g220)
    c: Block(g226)
    c: Block(g232)
    c: Block(g238)
    c: Coincident(g241,g226)
    c: Coincident(g241,g220)
    c: Horizontal(g241)
    c: Block(g183)
    c: Weight(g242) = 1
    c: Equal(g242,g243)
    c: Equal(g242,g244)
    c: InternalAlignment(g242,g245)
    c: InternalAlignment(g243,g245)
    c: InternalAlignment(g244,g245)
    c: InternalAlignment(g246,g245)
    c: InternalAlignment(g247,g245)
    c: Weight(g248) = 1
    c: Equal(g248,g249)
    c: Equal(g248,g250)
    c: InternalAlignment(g248,g251)
    c: InternalAlignment(g249,g251)
    c: InternalAlignment(g250,g251)
    c: InternalAlignment(g252,g251)
    c: InternalAlignment(g253,g251)
    c: Block(g245)
    c: Block(g251)
    c: Coincident(g254,g245)
    c: Coincident(g254,g251)
    c: Weight(g255) = 1
    c: Equal(g255,g256)
    c: Equal(g255,g257)
    c: InternalAlignment(g255,g258)
    c: InternalAlignment(g256,g258)
    c: InternalAlignment(g257,g258)
    c: InternalAlignment(g259,g258)
    c: InternalAlignment(g260,g258)
    c: Weight(g261) = 1
    c: Equal(g261,g262)
    c: Equal(g261,g263)
    c: InternalAlignment(g261,g264)
    c: InternalAlignment(g262,g264)
    c: InternalAlignment(g263,g264)
    c: InternalAlignment(g265,g264)
    c: InternalAlignment(g266,g264)
    c: Weight(g267) = 1
    c: Equal(g267,g268)
    c: Equal(g267,g269)
    c: InternalAlignment(g267,g270)
    c: InternalAlignment(g268,g270)
    c: InternalAlignment(g269,g270)
    c: InternalAlignment(g271,g270)
    c: InternalAlignment(g272,g270)
    c: Block(g270)
    c: Block(g264)
    c: Block(g258)
    c: Coincident(g273,g264)
    c: Coincident(g273,g258)
    c: Coincident(g274,g258)
    c: Coincident(g274,g270)
    c: Vertical(g274)
    c: Coincident(g275,g270)
    c: Coincident(g275,g264)
    c: Horizontal(g275)
    c: Weight(g276) = 1
    c: Equal(g276,g277)
    c: InternalAlignment(g276,g278)
    c: InternalAlignment(g277,g278)
    c: InternalAlignment(g279,g278)
    c: InternalAlignment(g280,g278)
    c: Weight(g281) = 1
    c: InternalAlignment(g282,g284)
    c: InternalAlignment(g283,g284)
    c: InternalAlignment(g285,g284)
    c: InternalAlignment(g286,g284)
    c: Weight(g287) = 1
    c: Equal(g287,g288)
    c: Equal(g287,g289)
    c: InternalAlignment(g287,g290)
    c: InternalAlignment(g288,g290)
    c: InternalAlignment(g289,g290)
    c: InternalAlignment(g291,g290)
    c: InternalAlignment(g292,g290)
    c: Equal(g293,g294)
    c: Equal(g293,g295)
    c: InternalAlignment(g293,g296)
    c: InternalAlignment(g294,g296)
    c: InternalAlignment(g295,g296)
    c: InternalAlignment(g297,g296)
    c: InternalAlignment(g298,g296)
    c: Block(g284)
    c: Block(g290)
    c: Block(g296)
    c: Block(g278)
    c: Coincident(g299,g278)
    c: Coincident(g299,g284)
    c: Horizontal(g299)
    c: Coincident(g300,g284)
    c: Coincident(g300,g290)
    c: Vertical(g300)
    c: Coincident(g301,g290)
    c: Coincident(g301,g296)
    c: Horizontal(g301)
    c: Coincident(g302,g296)
    c: Coincident(g302,g278)
    c: Weight(g303) = 1
    c: Equal(g303,g304)
    c: Equal(g303,g305)
    c: InternalAlignment(g303,g306)
    c: InternalAlignment(g304,g306)
    c: InternalAlignment(g305,g306)
    c: InternalAlignment(g307,g306)
    c: InternalAlignment(g308,g306)
    c: Weight(g309) = 1
    c: Equal(g309,g310)
    c: Equal(g309,g311)
    c: InternalAlignment(g309,g312)
    c: InternalAlignment(g310,g312)
    c: InternalAlignment(g311,g312)
    c: InternalAlignment(g313,g312)
    c: InternalAlignment(g314,g312)
    c: Weight(g315) = 1
    c: Equal(g315,g316)
    c: Equal(g315,g317)
    c: InternalAlignment(g315,g318)
    c: InternalAlignment(g316,g318)
    c: InternalAlignment(g317,g318)
    c: InternalAlignment(g319,g318)
    c: InternalAlignment(g320,g318)
    c: Block(g318)
    c: Block(g312)
    c: Block(g306)
    c: Coincident(g321,g318)
    c: Coincident(g321,g312)
    c: Horizontal(g321)
    c: Coincident(g322,g312)
    c: Coincident(g322,g306)
    c: Vertical(g322)
    c: Coincident(g323,g306)
    c: Coincident(g323,g318)
    c: InternalAlignment(g324,g325)
    c: InternalAlignment(g326,g325)
    c: InternalAlignment(g327,g325)
    c: Block(g325)
    c: Equal(g328,g329)
    c: Equal(g328,g330)
    c: InternalAlignment(g328,g331)
    c: InternalAlignment(g329,g331)
    c: InternalAlignment(g330,g331)
    c: InternalAlignment(g332,g331)
    c: InternalAlignment(g333,g331)
    c: Block(g331)
    c: Coincident(g334,g325)
    c: Horizontal(g334)
    c: Block(g334)
    c: Coincident(g335,g325)
    c: Coincident(g335,g251)
    c: Vertical(g335)
    c: Coincident(g336,g331)
    c: Coincident(g336,g245)
    c: Vertical(g336)
    c: Block(g337)
    c: Block(g2)
    c: Distance(g335) = 119.89
    c: Coincident(g338,g337)
    c: Coincident(g338,g2)
    c: Coincident(g339,g2)
    c: Coincident(g339,g337)
    c: Block(g3)
    c: Block(g340)
    c: Coincident(g341,g340)
    c: Coincident(g341,g3)
    c: Coincident(g342,g340)
    c: Coincident(g342,g3)
    c: Block(g342)
    c: Block(g341)
    c: Weight(g343) = 1
    c: Equal(g343,g344)
    c: Equal(g343,g345)
    c: InternalAlignment(g343,g346)
    c: InternalAlignment(g344,g346)
    c: InternalAlignment(g345,g346)
    c: InternalAlignment(g347,g346)
    c: InternalAlignment(g348,g346)
    c: Weight(g349) = 1
    c: Equal(g349,g350)
    c: Equal(g349,g351)
    c: InternalAlignment(g349,g352)
    c: InternalAlignment(g350,g352)
    c: InternalAlignment(g351,g352)
    c: InternalAlignment(g353,g352)
    c: InternalAlignment(g354,g352)
    c: Weight(g355) = 1
    c: Equal(g355,g356)
    c: Equal(g355,g357)
    c: InternalAlignment(g355,g358)
    c: InternalAlignment(g356,g358)
    c: InternalAlignment(g357,g358)
    c: InternalAlignment(g359,g358)
    c: InternalAlignment(g360,g358)
    c: Weight(g361) = 1
    c: Equal(g361,g362)
    c: Equal(g361,g363)
    c: InternalAlignment(g361,g364)
    c: InternalAlignment(g362,g364)
    c: InternalAlignment(g363,g364)
    c: InternalAlignment(g365,g364)
    c: InternalAlignment(g366,g364)
    c: Block(g364)
    c: Block(g358)
    c: Block(g352)
    c: Block(g346)
    c: Coincident(g367,g364)
    c: Coincident(g367,g346)
    c: Vertical(g367)
    c: Coincident(g368,g346)
    c: Coincident(g368,g352)
    c: Coincident(g369,g352)
    c: Coincident(g369,g358)
    c: Vertical(g369)
    c: Coincident(g370,g358)
    c: Coincident(g370,g364)
    c: Horizontal(g370)
    c: Vertical(g371)
    c: Vertical(g372)
    c: Vertical(g373)
    c: Vertical(g374)
    c: Coincident(g375,g0)
    c: Coincident(g375,g1)
    c: Horizontal(g375)
    c: Block(g375)
    c: Distance(g375) = 450
    c: Block(g373)
    c: Block(g371)
    c: Block(g372)
    c: Block(g374)
    c: Distance(g0) = 240
    c: Horizontal(g376)
    c: Distance(g376) = 12
    c: Coincident(g376,g371)
    c: Vertical(g377)
    c: Distance(g377) = 12
    c: Coincident(g377,g371)
    c: Coincident(g378,g376)
    c: Vertical(g378)
    c: Horizontal(g379)
    c: Vertical(g380)
    c: Distance(g380) = 6
    c: Coincident(g380,g376)
    c: Coincident(g379,g376)
    c: Block(g378)
    c: Coincident(g381,g378)
    c: Horizontal(g381)
    c: Distance(g381) = 6
FEATURE [Part::Extrusion] Extrude005
  Base = -> Sketch003
  Dir = (0,0,1)
  DirMode = 2
  FaceMakerClass = Part::FaceMakerBullseye
  LengthFwd = 24
  LengthRev = 0
  Solid = true
  Symmetric = false
